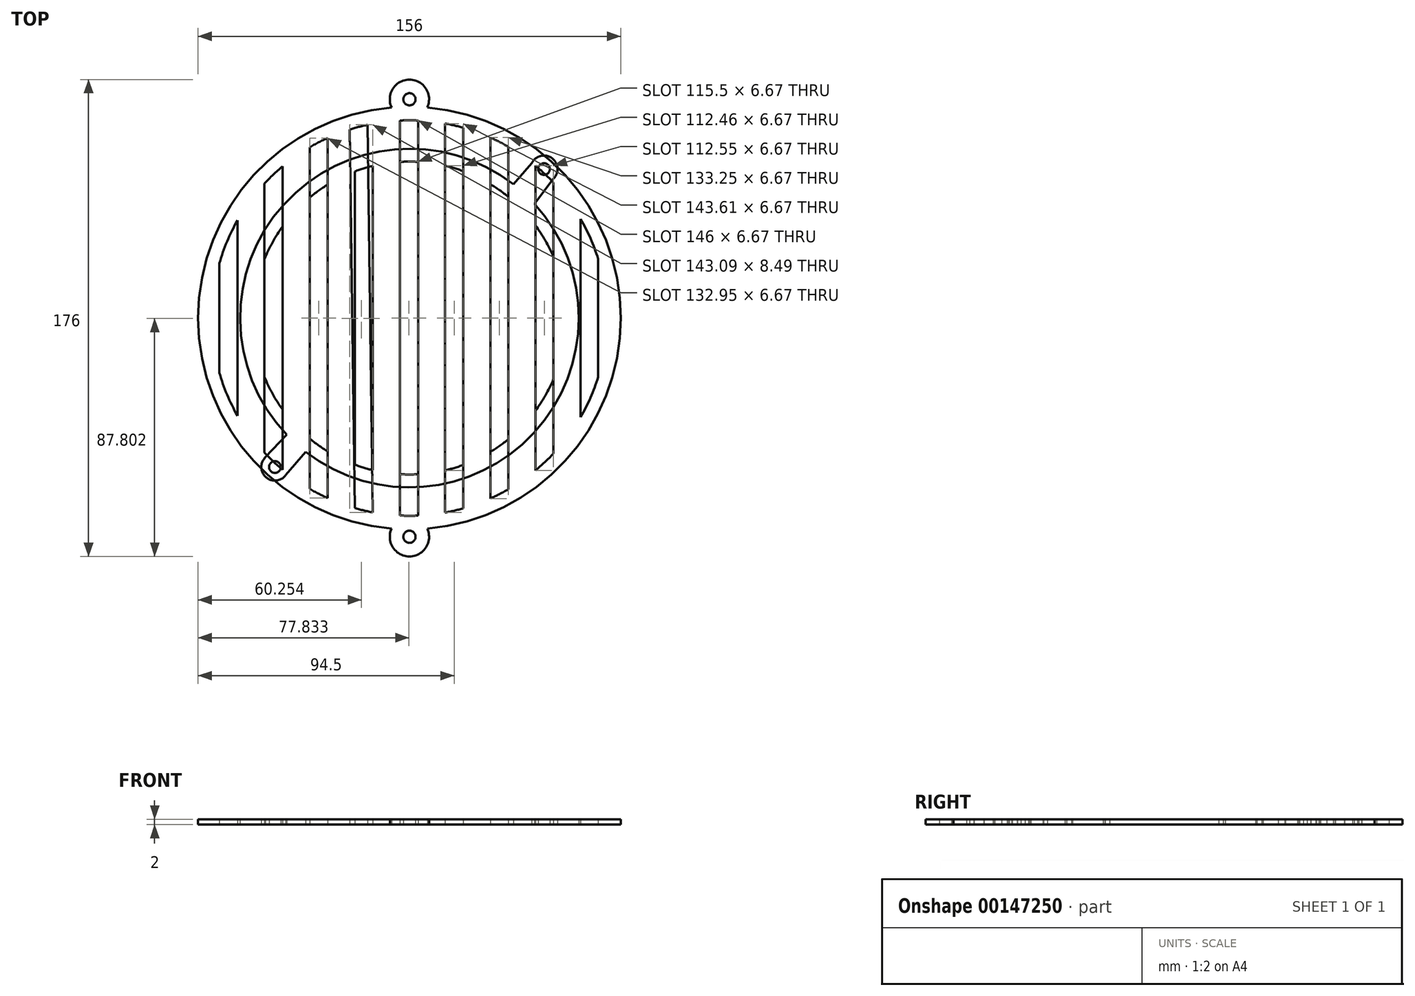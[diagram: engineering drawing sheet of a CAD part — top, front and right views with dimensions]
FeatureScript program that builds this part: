
annotation { "Feature Type Name" : "Feature", "Feature Type Description" : "" }
export const myFeature = defineFeature(function(context is Context, id is Id, definition is map)
    precondition{}
    {
        {
            var Q0;
            Q0=qCreatedBy(makeId("Top.planeOp"),FACE);
            var sketch = newSketch(context, id + "F0", { "sketchPlane" : qUnion([Q0])});
            skLineSegment(sketch, "E0.bottom", {"start": v(2, 0) * mm, "end": v(21.33, 0) * mm});
            skLineSegment(sketch, "E0.left", {"start": v(0, 2) * mm, "end": v(0, 2022) * mm});
            skLineSegment(sketch, "E0.right", {"start": v(409.5, 3.34) * mm, "end": v(409.5, 2020.66) * mm});
            skLineSegment(sketch, "E1", {"start": v(13.33, 12) * mm, "end": v(13.33, 2020) * mm, "construction": true});
            skLineSegment(sketch, "E2.0", {"start": v(23.33, 12) * mm, "end": v(23.33, 2020) * mm, "construction": true});
            skLineSegment(sketch, "E3.bottom", {"start": v(15.83, 22.83) * mm, "end": v(20.83, 22.83) * mm, "construction": true});
            skLineSegment(sketch, "E3.top", {"start": v(15.83, 17.83) * mm, "end": v(20.83, 17.83) * mm, "construction": true});
            skLineSegment(sketch, "E3.left", {"start": v(15.83, 22.83) * mm, "end": v(15.83, 17.83) * mm, "construction": true});
            skLineSegment(sketch, "E3.right", {"start": v(20.83, 22.83) * mm, "end": v(20.83, 17.83) * mm, "construction": true});
            skLineSegment(sketch, "E4", {"start": v(18.33, 17.83) * mm, "end": v(18.33, 22.83) * mm, "construction": true});
            skLineSegment(sketch, "E5", {"start": v(15.83, 20.33) * mm, "end": v(20.83, 20.33) * mm, "construction": true});
            skLineSegment(sketch, "E6", {"start": v(10, 0) * mm, "end": v(10, 28.72) * mm, "construction": true});
            skLineSegment(sketch, "E7", {"start": v(25.33, 12) * mm, "end": v(28, 12) * mm});
            skLineSegment(sketch, "E8", {"start": v(23.33, 10) * mm, "end": v(23.33, 2) * mm});
            skPoint(sketch, "E9.orphan", {"position": v(0, 12) * mm});
            skLineSegment(sketch, "E10", {"start": v(30, 10) * mm, "end": v(30, 2) * mm});
            skPoint(sketch, "E11.visualSharp", {"position": v(23.33, 12) * mm});
            skArc(sketch, "E11.filletArc", {"start": v(25.33, 12) * mm, "mid": v(23.92, 11.41) * mm, "end": v(23.33, 10) * mm});
            skPoint(sketch, "E12.visualSharp", {"position": v(30, 12) * mm});
            skArc(sketch, "E12.filletArc", {"start": v(30, 10) * mm, "mid": v(29.41, 11.41) * mm, "end": v(28, 12) * mm});
            skLineSegment(sketch, "E13.trimOffspring", {"start": v(32, 0) * mm, "end": v(38, 0) * mm});
            skPoint(sketch, "E14.visualSharp", {"position": v(23.33, 0) * mm});
            skArc(sketch, "E14.filletArc", {"start": v(21.33, 0) * mm, "mid": v(22.75, 0.59) * mm, "end": v(23.33, 2) * mm});
            skPoint(sketch, "E15.visualSharp", {"position": v(30, 0) * mm});
            skArc(sketch, "E15.filletArc", {"start": v(30, 2) * mm, "mid": v(30.59, 0.59) * mm, "end": v(32, 0) * mm});
            skLineSegment(sketch, "E16.1.0.0", {"start": v(42, 12) * mm, "end": v(44.67, 12) * mm});
            skArc(sketch, "E16.1.0.1", {"start": v(38, 0) * mm, "mid": v(39.41, 0.59) * mm, "end": v(40, 2) * mm});
            skLineSegment(sketch, "E16.1.0.2", {"start": v(40, 10) * mm, "end": v(40, 2) * mm});
            skArc(sketch, "E16.1.0.3", {"start": v(46.67, 10) * mm, "mid": v(46.08, 11.41) * mm, "end": v(44.67, 12) * mm});
            skPoint(sketch, "E16.1.0.4", {"position": v(46.67, 0) * mm});
            skPoint(sketch, "E16.1.0.5", {"position": v(40, 12) * mm});
            skPoint(sketch, "E16.1.0.6", {"position": v(40, 0) * mm});
            skLineSegment(sketch, "E16.1.0.7", {"start": v(46.67, 10) * mm, "end": v(46.67, 2) * mm});
            skArc(sketch, "E16.1.0.8", {"start": v(46.67, 2) * mm, "mid": v(47.25, 0.59) * mm, "end": v(48.67, 0) * mm});
            skArc(sketch, "E16.1.0.9", {"start": v(42, 12) * mm, "mid": v(40.59, 11.41) * mm, "end": v(40, 10) * mm});
            skPoint(sketch, "E16.1.0.10", {"position": v(46.67, 12) * mm});
            skLineSegment(sketch, "E16.1.0.11", {"start": v(48.67, 0) * mm, "end": v(54.67, 0) * mm});
            skLineSegment(sketch, "E16.2.0.0", {"start": v(58.67, 12) * mm, "end": v(61.33, 12) * mm});
            skArc(sketch, "E16.2.0.1", {"start": v(54.67, 0) * mm, "mid": v(56.08, 0.59) * mm, "end": v(56.67, 2) * mm});
            skLineSegment(sketch, "E16.2.0.2", {"start": v(56.67, 10) * mm, "end": v(56.67, 2) * mm});
            skArc(sketch, "E16.2.0.3", {"start": v(63.33, 10) * mm, "mid": v(62.75, 11.41) * mm, "end": v(61.33, 12) * mm});
            skPoint(sketch, "E16.2.0.4", {"position": v(63.33, 0) * mm});
            skPoint(sketch, "E16.2.0.5", {"position": v(56.67, 12) * mm});
            skPoint(sketch, "E16.2.0.6", {"position": v(56.67, 0) * mm});
            skLineSegment(sketch, "E16.2.0.7", {"start": v(63.33, 10) * mm, "end": v(63.33, 2) * mm});
            skArc(sketch, "E16.2.0.8", {"start": v(63.33, 2) * mm, "mid": v(63.92, 0.59) * mm, "end": v(65.33, 0) * mm});
            skArc(sketch, "E16.2.0.9", {"start": v(58.67, 12) * mm, "mid": v(57.25, 11.41) * mm, "end": v(56.67, 10) * mm});
            skPoint(sketch, "E16.2.0.10", {"position": v(63.33, 12) * mm});
            skLineSegment(sketch, "E16.2.0.11", {"start": v(65.33, 0) * mm, "end": v(71.33, 0) * mm});
            skLineSegment(sketch, "E16.3.0.0", {"start": v(75.33, 12) * mm, "end": v(78, 12) * mm});
            skArc(sketch, "E16.3.0.1", {"start": v(71.33, 0) * mm, "mid": v(72.75, 0.59) * mm, "end": v(73.33, 2) * mm});
            skLineSegment(sketch, "E16.3.0.2", {"start": v(73.33, 10) * mm, "end": v(73.33, 2) * mm});
            skArc(sketch, "E16.3.0.3", {"start": v(80, 10) * mm, "mid": v(79.41, 11.41) * mm, "end": v(78, 12) * mm});
            skPoint(sketch, "E16.3.0.4", {"position": v(80, 0) * mm});
            skPoint(sketch, "E16.3.0.5", {"position": v(73.33, 12) * mm});
            skPoint(sketch, "E16.3.0.6", {"position": v(73.33, 0) * mm});
            skLineSegment(sketch, "E16.3.0.7", {"start": v(80, 10) * mm, "end": v(80, 2) * mm});
            skArc(sketch, "E16.3.0.8", {"start": v(80, 2) * mm, "mid": v(80.59, 0.59) * mm, "end": v(82, 0) * mm});
            skArc(sketch, "E16.3.0.9", {"start": v(75.33, 12) * mm, "mid": v(73.92, 11.41) * mm, "end": v(73.33, 10) * mm});
            skPoint(sketch, "E16.3.0.10", {"position": v(80, 12) * mm});
            skLineSegment(sketch, "E16.3.0.11", {"start": v(82, 0) * mm, "end": v(88, 0) * mm});
            skLineSegment(sketch, "E16.4.0.0", {"start": v(92, 12) * mm, "end": v(94.67, 12) * mm});
            skArc(sketch, "E16.4.0.1", {"start": v(88, 0) * mm, "mid": v(89.41, 0.59) * mm, "end": v(90, 2) * mm});
            skLineSegment(sketch, "E16.4.0.2", {"start": v(90, 10) * mm, "end": v(90, 2) * mm});
            skArc(sketch, "E16.4.0.3", {"start": v(96.67, 10) * mm, "mid": v(96.08, 11.41) * mm, "end": v(94.67, 12) * mm});
            skPoint(sketch, "E16.4.0.4", {"position": v(96.67, 0) * mm});
            skPoint(sketch, "E16.4.0.5", {"position": v(90, 12) * mm});
            skPoint(sketch, "E16.4.0.6", {"position": v(90, 0) * mm});
            skLineSegment(sketch, "E16.4.0.7", {"start": v(96.67, 10) * mm, "end": v(96.67, 2) * mm});
            skArc(sketch, "E16.4.0.8", {"start": v(96.67, 2) * mm, "mid": v(97.25, 0.59) * mm, "end": v(98.67, 0) * mm});
            skArc(sketch, "E16.4.0.9", {"start": v(92, 12) * mm, "mid": v(90.59, 11.41) * mm, "end": v(90, 10) * mm});
            skPoint(sketch, "E16.4.0.10", {"position": v(96.67, 12) * mm});
            skLineSegment(sketch, "E16.4.0.11", {"start": v(98.67, 0) * mm, "end": v(104.67, 0) * mm});
            skLineSegment(sketch, "E16.5.0.0", {"start": v(108.67, 12) * mm, "end": v(111.33, 12) * mm});
            skArc(sketch, "E16.5.0.1", {"start": v(104.67, 0) * mm, "mid": v(106.08, 0.59) * mm, "end": v(106.67, 2) * mm});
            skLineSegment(sketch, "E16.5.0.2", {"start": v(106.67, 10) * mm, "end": v(106.67, 2) * mm});
            skArc(sketch, "E16.5.0.3", {"start": v(113.33, 10) * mm, "mid": v(112.75, 11.41) * mm, "end": v(111.33, 12) * mm});
            skPoint(sketch, "E16.5.0.4", {"position": v(113.33, 0) * mm});
            skPoint(sketch, "E16.5.0.5", {"position": v(106.67, 12) * mm});
            skPoint(sketch, "E16.5.0.6", {"position": v(106.67, 0) * mm});
            skLineSegment(sketch, "E16.5.0.7", {"start": v(113.33, 10) * mm, "end": v(113.33, 2) * mm});
            skArc(sketch, "E16.5.0.8", {"start": v(113.33, 2) * mm, "mid": v(113.92, 0.59) * mm, "end": v(115.33, 0) * mm});
            skArc(sketch, "E16.5.0.9", {"start": v(108.67, 12) * mm, "mid": v(107.25, 11.41) * mm, "end": v(106.67, 10) * mm});
            skPoint(sketch, "E16.5.0.10", {"position": v(113.33, 12) * mm});
            skLineSegment(sketch, "E16.5.0.11", {"start": v(115.33, 0) * mm, "end": v(121.33, 0) * mm});
            skLineSegment(sketch, "E16.6.0.0", {"start": v(125.33, 12) * mm, "end": v(128, 12) * mm});
            skArc(sketch, "E16.6.0.1", {"start": v(121.33, 0) * mm, "mid": v(122.75, 0.59) * mm, "end": v(123.33, 2) * mm});
            skLineSegment(sketch, "E16.6.0.2", {"start": v(123.33, 10) * mm, "end": v(123.33, 2) * mm});
            skArc(sketch, "E16.6.0.3", {"start": v(130, 10) * mm, "mid": v(129.41, 11.41) * mm, "end": v(128, 12) * mm});
            skPoint(sketch, "E16.6.0.4", {"position": v(130, 0) * mm});
            skPoint(sketch, "E16.6.0.5", {"position": v(123.33, 12) * mm});
            skPoint(sketch, "E16.6.0.6", {"position": v(123.33, 0) * mm});
            skLineSegment(sketch, "E16.6.0.7", {"start": v(130, 10) * mm, "end": v(130, 2) * mm});
            skArc(sketch, "E16.6.0.8", {"start": v(130, 2) * mm, "mid": v(130.59, 0.59) * mm, "end": v(132, 0) * mm});
            skArc(sketch, "E16.6.0.9", {"start": v(125.33, 12) * mm, "mid": v(123.92, 11.41) * mm, "end": v(123.33, 10) * mm});
            skPoint(sketch, "E16.6.0.10", {"position": v(130, 12) * mm});
            skLineSegment(sketch, "E16.6.0.11", {"start": v(132, 0) * mm, "end": v(138, 0) * mm});
            skLineSegment(sketch, "E16.7.0.0", {"start": v(142, 12) * mm, "end": v(144.67, 12) * mm});
            skArc(sketch, "E16.7.0.1", {"start": v(138, 0) * mm, "mid": v(139.41, 0.59) * mm, "end": v(140, 2) * mm});
            skLineSegment(sketch, "E16.7.0.2", {"start": v(140, 10) * mm, "end": v(140, 2) * mm});
            skArc(sketch, "E16.7.0.3", {"start": v(146.67, 10) * mm, "mid": v(146.08, 11.41) * mm, "end": v(144.67, 12) * mm});
            skPoint(sketch, "E16.7.0.4", {"position": v(146.67, 0) * mm});
            skPoint(sketch, "E16.7.0.5", {"position": v(140, 12) * mm});
            skPoint(sketch, "E16.7.0.6", {"position": v(140, 0) * mm});
            skLineSegment(sketch, "E16.7.0.7", {"start": v(146.67, 10) * mm, "end": v(146.67, 2) * mm});
            skArc(sketch, "E16.7.0.8", {"start": v(146.67, 2) * mm, "mid": v(147.25, 0.59) * mm, "end": v(148.67, 0) * mm});
            skArc(sketch, "E16.7.0.9", {"start": v(142, 12) * mm, "mid": v(140.59, 11.41) * mm, "end": v(140, 10) * mm});
            skPoint(sketch, "E16.7.0.10", {"position": v(146.67, 12) * mm});
            skLineSegment(sketch, "E16.7.0.11", {"start": v(148.67, 0) * mm, "end": v(154.67, 0) * mm});
            skLineSegment(sketch, "E16.8.0.0", {"start": v(158.67, 12) * mm, "end": v(161.33, 12) * mm});
            skArc(sketch, "E16.8.0.1", {"start": v(154.67, 0) * mm, "mid": v(156.08, 0.59) * mm, "end": v(156.67, 2) * mm});
            skLineSegment(sketch, "E16.8.0.2", {"start": v(156.67, 10) * mm, "end": v(156.67, 2) * mm});
            skArc(sketch, "E16.8.0.3", {"start": v(163.33, 10) * mm, "mid": v(162.75, 11.41) * mm, "end": v(161.33, 12) * mm});
            skPoint(sketch, "E16.8.0.4", {"position": v(163.33, 0) * mm});
            skPoint(sketch, "E16.8.0.5", {"position": v(156.67, 12) * mm});
            skPoint(sketch, "E16.8.0.6", {"position": v(156.67, 0) * mm});
            skLineSegment(sketch, "E16.8.0.7", {"start": v(163.33, 10) * mm, "end": v(163.33, 2) * mm});
            skArc(sketch, "E16.8.0.8", {"start": v(163.33, 2) * mm, "mid": v(163.92, 0.59) * mm, "end": v(165.33, 0) * mm});
            skArc(sketch, "E16.8.0.9", {"start": v(158.67, 12) * mm, "mid": v(157.25, 11.41) * mm, "end": v(156.67, 10) * mm});
            skPoint(sketch, "E16.8.0.10", {"position": v(163.33, 12) * mm});
            skLineSegment(sketch, "E16.8.0.11", {"start": v(165.33, 0) * mm, "end": v(171.33, 0) * mm});
            skLineSegment(sketch, "E16.9.0.0", {"start": v(175.33, 12) * mm, "end": v(178, 12) * mm});
            skArc(sketch, "E16.9.0.1", {"start": v(171.33, 0) * mm, "mid": v(172.75, 0.59) * mm, "end": v(173.33, 2) * mm});
            skLineSegment(sketch, "E16.9.0.2", {"start": v(173.33, 10) * mm, "end": v(173.33, 2) * mm});
            skArc(sketch, "E16.9.0.3", {"start": v(180, 10) * mm, "mid": v(179.41, 11.41) * mm, "end": v(178, 12) * mm});
            skPoint(sketch, "E16.9.0.4", {"position": v(180, 0) * mm});
            skPoint(sketch, "E16.9.0.5", {"position": v(173.33, 12) * mm});
            skPoint(sketch, "E16.9.0.6", {"position": v(173.33, 0) * mm});
            skLineSegment(sketch, "E16.9.0.7", {"start": v(180, 10) * mm, "end": v(180, 2) * mm});
            skArc(sketch, "E16.9.0.8", {"start": v(180, 2) * mm, "mid": v(180.59, 0.59) * mm, "end": v(182, 0) * mm});
            skArc(sketch, "E16.9.0.9", {"start": v(175.33, 12) * mm, "mid": v(173.92, 11.41) * mm, "end": v(173.33, 10) * mm});
            skPoint(sketch, "E16.9.0.10", {"position": v(180, 12) * mm});
            skLineSegment(sketch, "E16.9.0.11", {"start": v(182, 0) * mm, "end": v(188, 0) * mm});
            skLineSegment(sketch, "E16.10.0.0", {"start": v(192, 12) * mm, "end": v(194.67, 12) * mm});
            skArc(sketch, "E16.10.0.1", {"start": v(188, 0) * mm, "mid": v(189.41, 0.59) * mm, "end": v(190, 2) * mm});
            skLineSegment(sketch, "E16.10.0.2", {"start": v(190, 10) * mm, "end": v(190, 2) * mm});
            skArc(sketch, "E16.10.0.3", {"start": v(196.67, 10) * mm, "mid": v(196.08, 11.41) * mm, "end": v(194.67, 12) * mm});
            skPoint(sketch, "E16.10.0.4", {"position": v(196.67, 0) * mm});
            skPoint(sketch, "E16.10.0.5", {"position": v(190, 12) * mm});
            skPoint(sketch, "E16.10.0.6", {"position": v(190, 0) * mm});
            skLineSegment(sketch, "E16.10.0.7", {"start": v(196.67, 10) * mm, "end": v(196.67, 2) * mm});
            skArc(sketch, "E16.10.0.8", {"start": v(196.67, 2) * mm, "mid": v(197.25, 0.59) * mm, "end": v(198.67, 0) * mm});
            skArc(sketch, "E16.10.0.9", {"start": v(192, 12) * mm, "mid": v(190.59, 11.41) * mm, "end": v(190, 10) * mm});
            skPoint(sketch, "E16.10.0.10", {"position": v(196.67, 12) * mm});
            skLineSegment(sketch, "E16.10.0.11", {"start": v(198.67, 0) * mm, "end": v(204.67, 0) * mm});
            skLineSegment(sketch, "E16.11.0.0", {"start": v(208.67, 12) * mm, "end": v(211.33, 12) * mm});
            skArc(sketch, "E16.11.0.1", {"start": v(204.67, 0) * mm, "mid": v(206.08, 0.59) * mm, "end": v(206.67, 2) * mm});
            skLineSegment(sketch, "E16.11.0.2", {"start": v(206.67, 10) * mm, "end": v(206.67, 2) * mm});
            skArc(sketch, "E16.11.0.3", {"start": v(213.33, 10) * mm, "mid": v(212.75, 11.41) * mm, "end": v(211.33, 12) * mm});
            skPoint(sketch, "E16.11.0.4", {"position": v(213.33, 0) * mm});
            skPoint(sketch, "E16.11.0.5", {"position": v(206.67, 12) * mm});
            skPoint(sketch, "E16.11.0.6", {"position": v(206.67, 0) * mm});
            skLineSegment(sketch, "E16.11.0.7", {"start": v(213.33, 10) * mm, "end": v(213.33, 2) * mm});
            skArc(sketch, "E16.11.0.8", {"start": v(213.33, 2) * mm, "mid": v(213.92, 0.59) * mm, "end": v(215.33, 0) * mm});
            skArc(sketch, "E16.11.0.9", {"start": v(208.67, 12) * mm, "mid": v(207.25, 11.41) * mm, "end": v(206.67, 10) * mm});
            skPoint(sketch, "E16.11.0.10", {"position": v(213.33, 12) * mm});
            skLineSegment(sketch, "E16.11.0.11", {"start": v(215.33, 0) * mm, "end": v(221.33, 0) * mm});
            skLineSegment(sketch, "E16.12.0.0", {"start": v(225.33, 12) * mm, "end": v(228, 12) * mm});
            skArc(sketch, "E16.12.0.1", {"start": v(221.33, 0) * mm, "mid": v(222.75, 0.59) * mm, "end": v(223.33, 2) * mm});
            skLineSegment(sketch, "E16.12.0.2", {"start": v(223.33, 10) * mm, "end": v(223.33, 2) * mm});
            skArc(sketch, "E16.12.0.3", {"start": v(230, 10) * mm, "mid": v(229.41, 11.41) * mm, "end": v(228, 12) * mm});
            skPoint(sketch, "E16.12.0.4", {"position": v(230, 0) * mm});
            skPoint(sketch, "E16.12.0.5", {"position": v(223.33, 12) * mm});
            skPoint(sketch, "E16.12.0.6", {"position": v(223.33, 0) * mm});
            skLineSegment(sketch, "E16.12.0.7", {"start": v(230, 10) * mm, "end": v(230, 2) * mm});
            skArc(sketch, "E16.12.0.8", {"start": v(230, 2) * mm, "mid": v(230.59, 0.59) * mm, "end": v(232, 0) * mm});
            skArc(sketch, "E16.12.0.9", {"start": v(225.33, 12) * mm, "mid": v(223.92, 11.41) * mm, "end": v(223.33, 10) * mm});
            skPoint(sketch, "E16.12.0.10", {"position": v(230, 12) * mm});
            skLineSegment(sketch, "E16.12.0.11", {"start": v(232, 0) * mm, "end": v(238, 0) * mm});
            skLineSegment(sketch, "E16.13.0.0", {"start": v(242, 12) * mm, "end": v(244.67, 12) * mm});
            skArc(sketch, "E16.13.0.1", {"start": v(238, 0) * mm, "mid": v(239.41, 0.59) * mm, "end": v(240, 2) * mm});
            skLineSegment(sketch, "E16.13.0.2", {"start": v(240, 10) * mm, "end": v(240, 2) * mm});
            skArc(sketch, "E16.13.0.3", {"start": v(246.67, 10) * mm, "mid": v(246.08, 11.41) * mm, "end": v(244.67, 12) * mm});
            skPoint(sketch, "E16.13.0.4", {"position": v(246.67, 0) * mm});
            skPoint(sketch, "E16.13.0.5", {"position": v(240, 12) * mm});
            skPoint(sketch, "E16.13.0.6", {"position": v(240, 0) * mm});
            skLineSegment(sketch, "E16.13.0.7", {"start": v(246.67, 10) * mm, "end": v(246.67, 2) * mm});
            skArc(sketch, "E16.13.0.8", {"start": v(246.67, 2) * mm, "mid": v(247.25, 0.59) * mm, "end": v(248.67, 0) * mm});
            skArc(sketch, "E16.13.0.9", {"start": v(242, 12) * mm, "mid": v(240.59, 11.41) * mm, "end": v(240, 10) * mm});
            skPoint(sketch, "E16.13.0.10", {"position": v(246.67, 12) * mm});
            skLineSegment(sketch, "E16.13.0.11", {"start": v(248.67, 0) * mm, "end": v(254.67, 0) * mm});
            skLineSegment(sketch, "E16.14.0.0", {"start": v(258.67, 12) * mm, "end": v(261.33, 12) * mm});
            skArc(sketch, "E16.14.0.1", {"start": v(254.67, 0) * mm, "mid": v(256.08, 0.59) * mm, "end": v(256.67, 2) * mm});
            skLineSegment(sketch, "E16.14.0.2", {"start": v(256.67, 10) * mm, "end": v(256.67, 2) * mm});
            skArc(sketch, "E16.14.0.3", {"start": v(263.33, 10) * mm, "mid": v(262.75, 11.41) * mm, "end": v(261.33, 12) * mm});
            skPoint(sketch, "E16.14.0.4", {"position": v(263.33, 0) * mm});
            skPoint(sketch, "E16.14.0.5", {"position": v(256.67, 12) * mm});
            skPoint(sketch, "E16.14.0.6", {"position": v(256.67, 0) * mm});
            skLineSegment(sketch, "E16.14.0.7", {"start": v(263.33, 10) * mm, "end": v(263.33, 2) * mm});
            skArc(sketch, "E16.14.0.8", {"start": v(263.33, 2) * mm, "mid": v(263.92, 0.59) * mm, "end": v(265.33, 0) * mm});
            skArc(sketch, "E16.14.0.9", {"start": v(258.67, 12) * mm, "mid": v(257.25, 11.41) * mm, "end": v(256.67, 10) * mm});
            skPoint(sketch, "E16.14.0.10", {"position": v(263.33, 12) * mm});
            skLineSegment(sketch, "E16.14.0.11", {"start": v(265.33, 0) * mm, "end": v(271.33, 0) * mm});
            skLineSegment(sketch, "E16.15.0.0", {"start": v(275.33, 12) * mm, "end": v(278, 12) * mm});
            skArc(sketch, "E16.15.0.1", {"start": v(271.33, 0) * mm, "mid": v(272.75, 0.59) * mm, "end": v(273.33, 2) * mm});
            skLineSegment(sketch, "E16.15.0.2", {"start": v(273.33, 10) * mm, "end": v(273.33, 2) * mm});
            skArc(sketch, "E16.15.0.3", {"start": v(280, 10) * mm, "mid": v(279.41, 11.41) * mm, "end": v(278, 12) * mm});
            skPoint(sketch, "E16.15.0.4", {"position": v(280, 0) * mm});
            skPoint(sketch, "E16.15.0.5", {"position": v(273.33, 12) * mm});
            skPoint(sketch, "E16.15.0.6", {"position": v(273.33, 0) * mm});
            skLineSegment(sketch, "E16.15.0.7", {"start": v(280, 10) * mm, "end": v(280, 2) * mm});
            skArc(sketch, "E16.15.0.8", {"start": v(280, 2) * mm, "mid": v(280.59, 0.59) * mm, "end": v(282, 0) * mm});
            skArc(sketch, "E16.15.0.9", {"start": v(275.33, 12) * mm, "mid": v(273.92, 11.41) * mm, "end": v(273.33, 10) * mm});
            skPoint(sketch, "E16.15.0.10", {"position": v(280, 12) * mm});
            skLineSegment(sketch, "E16.15.0.11", {"start": v(282, 0) * mm, "end": v(288, 0) * mm});
            skLineSegment(sketch, "E16.16.0.0", {"start": v(292, 12) * mm, "end": v(294.67, 12) * mm});
            skArc(sketch, "E16.16.0.1", {"start": v(288, 0) * mm, "mid": v(289.41, 0.59) * mm, "end": v(290, 2) * mm});
            skLineSegment(sketch, "E16.16.0.2", {"start": v(290, 10) * mm, "end": v(290, 2) * mm});
            skArc(sketch, "E16.16.0.3", {"start": v(296.67, 10) * mm, "mid": v(296.08, 11.41) * mm, "end": v(294.67, 12) * mm});
            skPoint(sketch, "E16.16.0.4", {"position": v(296.67, 0) * mm});
            skPoint(sketch, "E16.16.0.5", {"position": v(290, 12) * mm});
            skPoint(sketch, "E16.16.0.6", {"position": v(290, 0) * mm});
            skLineSegment(sketch, "E16.16.0.7", {"start": v(296.67, 10) * mm, "end": v(296.67, 2) * mm});
            skArc(sketch, "E16.16.0.8", {"start": v(296.67, 2) * mm, "mid": v(297.25, 0.59) * mm, "end": v(298.67, 0) * mm});
            skArc(sketch, "E16.16.0.9", {"start": v(292, 12) * mm, "mid": v(290.59, 11.41) * mm, "end": v(290, 10) * mm});
            skPoint(sketch, "E16.16.0.10", {"position": v(296.67, 12) * mm});
            skLineSegment(sketch, "E16.16.0.11", {"start": v(298.67, 0) * mm, "end": v(304.67, 0) * mm});
            skLineSegment(sketch, "E16.17.0.0", {"start": v(308.67, 12) * mm, "end": v(311.33, 12) * mm});
            skArc(sketch, "E16.17.0.1", {"start": v(304.67, 0) * mm, "mid": v(306.08, 0.59) * mm, "end": v(306.67, 2) * mm});
            skLineSegment(sketch, "E16.17.0.2", {"start": v(306.67, 10) * mm, "end": v(306.67, 2) * mm});
            skArc(sketch, "E16.17.0.3", {"start": v(313.33, 10) * mm, "mid": v(312.75, 11.41) * mm, "end": v(311.33, 12) * mm});
            skPoint(sketch, "E16.17.0.4", {"position": v(313.33, 0) * mm});
            skPoint(sketch, "E16.17.0.5", {"position": v(306.67, 12) * mm});
            skPoint(sketch, "E16.17.0.6", {"position": v(306.67, 0) * mm});
            skLineSegment(sketch, "E16.17.0.7", {"start": v(313.33, 10) * mm, "end": v(313.33, 2) * mm});
            skArc(sketch, "E16.17.0.8", {"start": v(313.33, 2) * mm, "mid": v(313.92, 0.59) * mm, "end": v(315.33, 0) * mm});
            skArc(sketch, "E16.17.0.9", {"start": v(308.67, 12) * mm, "mid": v(307.25, 11.41) * mm, "end": v(306.67, 10) * mm});
            skPoint(sketch, "E16.17.0.10", {"position": v(313.33, 12) * mm});
            skLineSegment(sketch, "E16.17.0.11", {"start": v(315.33, 0) * mm, "end": v(321.33, 0) * mm});
            skLineSegment(sketch, "E16.18.0.0", {"start": v(325.33, 12) * mm, "end": v(328, 12) * mm});
            skArc(sketch, "E16.18.0.1", {"start": v(321.33, 0) * mm, "mid": v(322.75, 0.59) * mm, "end": v(323.33, 2) * mm});
            skLineSegment(sketch, "E16.18.0.2", {"start": v(323.33, 10) * mm, "end": v(323.33, 2) * mm});
            skArc(sketch, "E16.18.0.3", {"start": v(330, 10) * mm, "mid": v(329.41, 11.41) * mm, "end": v(328, 12) * mm});
            skPoint(sketch, "E16.18.0.4", {"position": v(330, 0) * mm});
            skPoint(sketch, "E16.18.0.5", {"position": v(323.33, 12) * mm});
            skPoint(sketch, "E16.18.0.6", {"position": v(323.33, 0) * mm});
            skLineSegment(sketch, "E16.18.0.7", {"start": v(330, 10) * mm, "end": v(330, 2) * mm});
            skArc(sketch, "E16.18.0.8", {"start": v(330, 2) * mm, "mid": v(330.59, 0.59) * mm, "end": v(332, 0) * mm});
            skArc(sketch, "E16.18.0.9", {"start": v(325.33, 12) * mm, "mid": v(323.92, 11.41) * mm, "end": v(323.33, 10) * mm});
            skPoint(sketch, "E16.18.0.10", {"position": v(330, 12) * mm});
            skLineSegment(sketch, "E16.18.0.11", {"start": v(332, 0) * mm, "end": v(338, 0) * mm});
            skLineSegment(sketch, "E16.19.0.0", {"start": v(342, 12) * mm, "end": v(344.67, 12) * mm});
            skArc(sketch, "E16.19.0.1", {"start": v(338, 0) * mm, "mid": v(339.41, 0.59) * mm, "end": v(340, 2) * mm});
            skLineSegment(sketch, "E16.19.0.2", {"start": v(340, 10) * mm, "end": v(340, 2) * mm});
            skArc(sketch, "E16.19.0.3", {"start": v(346.67, 10) * mm, "mid": v(346.08, 11.41) * mm, "end": v(344.67, 12) * mm});
            skPoint(sketch, "E16.19.0.4", {"position": v(346.67, 0) * mm});
            skPoint(sketch, "E16.19.0.5", {"position": v(340, 12) * mm});
            skPoint(sketch, "E16.19.0.6", {"position": v(340, 0) * mm});
            skLineSegment(sketch, "E16.19.0.7", {"start": v(346.67, 10) * mm, "end": v(346.67, 2) * mm});
            skArc(sketch, "E16.19.0.8", {"start": v(346.67, 2) * mm, "mid": v(347.25, 0.59) * mm, "end": v(348.67, 0) * mm});
            skArc(sketch, "E16.19.0.9", {"start": v(342, 12) * mm, "mid": v(340.59, 11.41) * mm, "end": v(340, 10) * mm});
            skPoint(sketch, "E16.19.0.10", {"position": v(346.67, 12) * mm});
            skLineSegment(sketch, "E16.19.0.11", {"start": v(348.67, 0) * mm, "end": v(354.67, 0) * mm});
            skLineSegment(sketch, "E16.20.0.0", {"start": v(358.67, 12) * mm, "end": v(361.33, 12) * mm});
            skArc(sketch, "E16.20.0.1", {"start": v(354.67, 0) * mm, "mid": v(356.08, 0.59) * mm, "end": v(356.67, 2) * mm});
            skLineSegment(sketch, "E16.20.0.2", {"start": v(356.67, 10) * mm, "end": v(356.67, 2) * mm});
            skArc(sketch, "E16.20.0.3", {"start": v(363.33, 10) * mm, "mid": v(362.75, 11.41) * mm, "end": v(361.33, 12) * mm});
            skPoint(sketch, "E16.20.0.4", {"position": v(363.33, 0) * mm});
            skPoint(sketch, "E16.20.0.5", {"position": v(356.67, 12) * mm});
            skPoint(sketch, "E16.20.0.6", {"position": v(356.67, 0) * mm});
            skLineSegment(sketch, "E16.20.0.7", {"start": v(363.33, 10) * mm, "end": v(363.33, 2) * mm});
            skArc(sketch, "E16.20.0.8", {"start": v(363.33, 2) * mm, "mid": v(363.92, 0.59) * mm, "end": v(365.33, 0) * mm});
            skArc(sketch, "E16.20.0.9", {"start": v(358.67, 12) * mm, "mid": v(357.25, 11.41) * mm, "end": v(356.67, 10) * mm});
            skPoint(sketch, "E16.20.0.10", {"position": v(363.33, 12) * mm});
            skLineSegment(sketch, "E16.20.0.11", {"start": v(365.33, 0) * mm, "end": v(371.33, 0) * mm});
            skLineSegment(sketch, "E16.21.0.0", {"start": v(375.33, 12) * mm, "end": v(378, 12) * mm});
            skArc(sketch, "E16.21.0.1", {"start": v(371.33, 0) * mm, "mid": v(372.75, 0.59) * mm, "end": v(373.33, 2) * mm});
            skLineSegment(sketch, "E16.21.0.2", {"start": v(373.33, 10) * mm, "end": v(373.33, 2) * mm});
            skArc(sketch, "E16.21.0.3", {"start": v(380, 10) * mm, "mid": v(379.41, 11.41) * mm, "end": v(378, 12) * mm});
            skPoint(sketch, "E16.21.0.4", {"position": v(380, 0) * mm});
            skPoint(sketch, "E16.21.0.5", {"position": v(373.33, 12) * mm});
            skPoint(sketch, "E16.21.0.6", {"position": v(373.33, 0) * mm});
            skLineSegment(sketch, "E16.21.0.7", {"start": v(380, 10) * mm, "end": v(380, 2) * mm});
            skArc(sketch, "E16.21.0.8", {"start": v(380, 2) * mm, "mid": v(380.59, 0.59) * mm, "end": v(382, 0) * mm});
            skArc(sketch, "E16.21.0.9", {"start": v(375.33, 12) * mm, "mid": v(373.92, 11.41) * mm, "end": v(373.33, 10) * mm});
            skPoint(sketch, "E16.21.0.10", {"position": v(380, 12) * mm});
            skLineSegment(sketch, "E16.21.0.11", {"start": v(382, 0) * mm, "end": v(388, 0) * mm});
            skLineSegment(sketch, "E16.22.0.0", {"start": v(392, 12) * mm, "end": v(394.67, 12) * mm});
            skArc(sketch, "E16.22.0.1", {"start": v(388, 0) * mm, "mid": v(389.41, 0.59) * mm, "end": v(390, 2) * mm});
            skLineSegment(sketch, "E16.22.0.2", {"start": v(390, 10) * mm, "end": v(390, 2) * mm});
            skArc(sketch, "E16.22.0.3", {"start": v(396.67, 10) * mm, "mid": v(396.08, 11.41) * mm, "end": v(394.67, 12) * mm});
            skPoint(sketch, "E16.22.0.4", {"position": v(396.67, 0) * mm});
            skPoint(sketch, "E16.22.0.5", {"position": v(390, 12) * mm});
            skPoint(sketch, "E16.22.0.6", {"position": v(390, 0) * mm});
            skLineSegment(sketch, "E16.22.0.7", {"start": v(396.67, 10) * mm, "end": v(396.67, 2) * mm});
            skArc(sketch, "E16.22.0.8", {"start": v(396.67, 2) * mm, "mid": v(397.25, 0.59) * mm, "end": v(398.67, 0) * mm});
            skArc(sketch, "E16.22.0.9", {"start": v(392, 12) * mm, "mid": v(390.59, 11.41) * mm, "end": v(390, 10) * mm});
            skPoint(sketch, "E16.22.0.10", {"position": v(396.67, 12) * mm});
            skLineSegment(sketch, "E16.22.0.11", {"start": v(398.67, 0) * mm, "end": v(404.67, 0) * mm});
            skLineSegment(sketch, "E16.direction1", {"start": v(21.33, 0) * mm, "end": v(38, 0) * mm, "construction": true});
            skLineSegment(sketch, "E17", {"start": v(404.67, 0) * mm, "end": v(408.26, 1.49) * mm});
            skLineSegment(sketch, "E18", {"start": v(409.5, 1012) * mm, "end": v(322.2, 1012) * mm, "construction": true});
            skPoint(sketch, "E18.endSnap0", {"position": v(409.5, 1012) * mm});
            skLineSegment(sketch, "E19.MirrorCS", {"start": v(198.67, 2024) * mm, "end": v(204.67, 2024) * mm});
            skLineSegment(sketch, "E20.MirrorCS", {"start": v(175.33, 2012) * mm, "end": v(178, 2012) * mm});
            skLineSegment(sketch, "E21.MirrorCS", {"start": v(208.67, 2012) * mm, "end": v(211.33, 2012) * mm});
            skLineSegment(sketch, "E22.MirrorCS", {"start": v(165.33, 2024) * mm, "end": v(171.33, 2024) * mm});
            skLineSegment(sketch, "E23.MirrorCS", {"start": v(140, 2014) * mm, "end": v(140, 2022) * mm});
            skLineSegment(sketch, "E24.MirrorCS", {"start": v(192, 2012) * mm, "end": v(194.67, 2012) * mm});
            skLineSegment(sketch, "E25.MirrorCS", {"start": v(158.67, 2012) * mm, "end": v(161.33, 2012) * mm});
            skLineSegment(sketch, "E26.MirrorCS", {"start": v(125.33, 2012) * mm, "end": v(128, 2012) * mm});
            skLineSegment(sketch, "E27.MirrorCS", {"start": v(173.33, 2014) * mm, "end": v(173.33, 2022) * mm});
            skLineSegment(sketch, "E28.MirrorCS", {"start": v(132, 2024) * mm, "end": v(138, 2024) * mm});
            skLineSegment(sketch, "E29.MirrorCS", {"start": v(142, 2012) * mm, "end": v(144.67, 2012) * mm});
            skArc(sketch, "E30.MirrorCS", {"start": v(204.67, 2024) * mm, "mid": v(206.08, 2023.41) * mm, "end": v(206.67, 2022) * mm});
            skLineSegment(sketch, "E31.MirrorCS", {"start": v(108.67, 2012) * mm, "end": v(111.33, 2012) * mm});
            skLineSegment(sketch, "E32.MirrorCS", {"start": v(130, 2014) * mm, "end": v(130, 2022) * mm});
            skLineSegment(sketch, "E33.MirrorCS", {"start": v(163.33, 2014) * mm, "end": v(163.33, 2022) * mm});
            skArc(sketch, "E34.MirrorCS", {"start": v(196.67, 2014) * mm, "mid": v(196.08, 2012.59) * mm, "end": v(194.67, 2012) * mm});
            skArc(sketch, "E35.MirrorCS", {"start": v(163.33, 2014) * mm, "mid": v(162.75, 2012.59) * mm, "end": v(161.33, 2012) * mm});
            skArc(sketch, "E36.MirrorCS", {"start": v(130, 2014) * mm, "mid": v(129.41, 2012.59) * mm, "end": v(128, 2012) * mm});
            skLineSegment(sketch, "E37.MirrorCS", {"start": v(242, 2012) * mm, "end": v(244.67, 2012) * mm});
            skLineSegment(sketch, "E38.MirrorCS", {"start": v(206.67, 2014) * mm, "end": v(206.67, 2022) * mm});
            skLineSegment(sketch, "E39.MirrorCS", {"start": v(225.33, 2012) * mm, "end": v(228, 2012) * mm});
            skArc(sketch, "E40.MirrorCS", {"start": v(138, 2024) * mm, "mid": v(139.41, 2023.41) * mm, "end": v(140, 2022) * mm});
            skLineSegment(sketch, "E41.MirrorCS", {"start": v(232, 2024) * mm, "end": v(238, 2024) * mm});
            skArc(sketch, "E42.MirrorCS", {"start": v(171.33, 2024) * mm, "mid": v(172.75, 2023.41) * mm, "end": v(173.33, 2022) * mm});
            skLineSegment(sketch, "E43.MirrorCS", {"start": v(98.67, 2024) * mm, "end": v(104.67, 2024) * mm});
            skLineSegment(sketch, "E44.MirrorCS", {"start": v(148.67, 2024) * mm, "end": v(154.67, 2024) * mm});
            skLineSegment(sketch, "E45.MirrorCS", {"start": v(182, 2024) * mm, "end": v(188, 2024) * mm});
            skLineSegment(sketch, "E46.MirrorCS", {"start": v(215.33, 2024) * mm, "end": v(221.33, 2024) * mm});
            skLineSegment(sketch, "E47.MirrorCS", {"start": v(115.33, 2024) * mm, "end": v(121.33, 2024) * mm});
            skLineSegment(sketch, "E48.MirrorCS", {"start": v(106.67, 2014) * mm, "end": v(106.67, 2022) * mm});
            skArc(sketch, "E49.MirrorCS", {"start": v(146.67, 2014) * mm, "mid": v(146.08, 2012.59) * mm, "end": v(144.67, 2012) * mm});
            skArc(sketch, "E50.MirrorCS", {"start": v(180, 2014) * mm, "mid": v(179.41, 2012.59) * mm, "end": v(178, 2012) * mm});
            skLineSegment(sketch, "E51.MirrorCS", {"start": v(146.67, 2014) * mm, "end": v(146.67, 2022) * mm});
            skLineSegment(sketch, "E52.MirrorCS", {"start": v(180, 2014) * mm, "end": v(180, 2022) * mm});
            skArc(sketch, "E53.MirrorCS", {"start": v(213.33, 2014) * mm, "mid": v(212.75, 2012.59) * mm, "end": v(211.33, 2012) * mm});
            skLineSegment(sketch, "E54.MirrorCS", {"start": v(213.33, 2014) * mm, "end": v(213.33, 2022) * mm});
            skLineSegment(sketch, "E55.MirrorCS", {"start": v(113.33, 2014) * mm, "end": v(113.33, 2022) * mm});
            skArc(sketch, "E56.MirrorCS", {"start": v(113.33, 2014) * mm, "mid": v(112.75, 2012.59) * mm, "end": v(111.33, 2012) * mm});
            skArc(sketch, "E57.MirrorCS", {"start": v(125.33, 2012) * mm, "mid": v(123.92, 2012.59) * mm, "end": v(123.33, 2014) * mm});
            skArc(sketch, "E58.MirrorCS", {"start": v(158.67, 2012) * mm, "mid": v(157.25, 2012.59) * mm, "end": v(156.67, 2014) * mm});
            skLineSegment(sketch, "E59.MirrorCS", {"start": v(265.33, 2024) * mm, "end": v(271.33, 2024) * mm});
            skLineSegment(sketch, "E60.MirrorCS", {"start": v(96.67, 2014) * mm, "end": v(96.67, 2022) * mm});
            skLineSegment(sketch, "E61.MirrorCS", {"start": v(196.67, 2014) * mm, "end": v(196.67, 2022) * mm});
            skArc(sketch, "E62.MirrorCS", {"start": v(230, 2014) * mm, "mid": v(229.41, 2012.59) * mm, "end": v(228, 2012) * mm});
            skLineSegment(sketch, "E63.MirrorCS", {"start": v(275.33, 2012) * mm, "end": v(278, 2012) * mm});
            skArc(sketch, "E64.MirrorCS", {"start": v(238, 2024) * mm, "mid": v(239.41, 2023.41) * mm, "end": v(240, 2022) * mm});
            skArc(sketch, "E65.MirrorCS", {"start": v(104.67, 2024) * mm, "mid": v(106.08, 2023.41) * mm, "end": v(106.67, 2022) * mm});
            skArc(sketch, "E66.MirrorCS", {"start": v(196.67, 2022) * mm, "mid": v(197.25, 2023.41) * mm, "end": v(198.67, 2024) * mm});
            skLineSegment(sketch, "E67.MirrorCS", {"start": v(190, 2014) * mm, "end": v(190, 2022) * mm});
            skLineSegment(sketch, "E68.MirrorCS", {"start": v(223.33, 2014) * mm, "end": v(223.33, 2022) * mm});
            skArc(sketch, "E69.MirrorCS", {"start": v(163.33, 2022) * mm, "mid": v(163.92, 2023.41) * mm, "end": v(165.33, 2024) * mm});
            skLineSegment(sketch, "E70.MirrorCS", {"start": v(156.67, 2014) * mm, "end": v(156.67, 2022) * mm});
            skLineSegment(sketch, "E71.MirrorCS", {"start": v(258.67, 2012) * mm, "end": v(261.33, 2012) * mm});
            skLineSegment(sketch, "E72.MirrorCS", {"start": v(92, 2012) * mm, "end": v(94.67, 2012) * mm});
            skArc(sketch, "E73.MirrorCS", {"start": v(192, 2012) * mm, "mid": v(190.59, 2012.59) * mm, "end": v(190, 2014) * mm});
            skLineSegment(sketch, "E74.MirrorCS", {"start": v(123.33, 2014) * mm, "end": v(123.33, 2022) * mm});
            skLineSegment(sketch, "E75.MirrorCS", {"start": v(273.33, 2014) * mm, "end": v(273.33, 2022) * mm});
            skLineSegment(sketch, "E76.MirrorCS", {"start": v(240, 2014) * mm, "end": v(240, 2022) * mm});
            skArc(sketch, "E77.MirrorCS", {"start": v(188, 2024) * mm, "mid": v(189.41, 2023.41) * mm, "end": v(190, 2022) * mm});
            skArc(sketch, "E78.MirrorCS", {"start": v(221.33, 2024) * mm, "mid": v(222.75, 2023.41) * mm, "end": v(223.33, 2022) * mm});
            skArc(sketch, "E79.MirrorCS", {"start": v(154.67, 2024) * mm, "mid": v(156.08, 2023.41) * mm, "end": v(156.67, 2022) * mm});
            skLineSegment(sketch, "E80.MirrorCS", {"start": v(248.67, 2024) * mm, "end": v(254.67, 2024) * mm});
            skArc(sketch, "E81.MirrorCS", {"start": v(130, 2022) * mm, "mid": v(130.59, 2023.41) * mm, "end": v(132, 2024) * mm});
            skArc(sketch, "E82.MirrorCS", {"start": v(121.33, 2024) * mm, "mid": v(122.75, 2023.41) * mm, "end": v(123.33, 2022) * mm});
            skArc(sketch, "E83.MirrorCS", {"start": v(246.67, 2014) * mm, "mid": v(246.08, 2012.59) * mm, "end": v(244.67, 2012) * mm});
            skArc(sketch, "E84.MirrorCS", {"start": v(142, 2012) * mm, "mid": v(140.59, 2012.59) * mm, "end": v(140, 2014) * mm});
            skArc(sketch, "E85.MirrorCS", {"start": v(208.67, 2012) * mm, "mid": v(207.25, 2012.59) * mm, "end": v(206.67, 2014) * mm});
            skArc(sketch, "E86.MirrorCS", {"start": v(180, 2022) * mm, "mid": v(180.59, 2023.41) * mm, "end": v(182, 2024) * mm});
            skArc(sketch, "E87.MirrorCS", {"start": v(213.33, 2022) * mm, "mid": v(213.92, 2023.41) * mm, "end": v(215.33, 2024) * mm});
            skArc(sketch, "E88.MirrorCS", {"start": v(113.33, 2022) * mm, "mid": v(113.92, 2023.41) * mm, "end": v(115.33, 2024) * mm});
            skArc(sketch, "E89.MirrorCS", {"start": v(175.33, 2012) * mm, "mid": v(173.92, 2012.59) * mm, "end": v(173.33, 2014) * mm});
            skArc(sketch, "E90.MirrorCS", {"start": v(146.67, 2022) * mm, "mid": v(147.25, 2023.41) * mm, "end": v(148.67, 2024) * mm});
            skLineSegment(sketch, "E91.MirrorCS", {"start": v(246.67, 2014) * mm, "end": v(246.67, 2022) * mm});
            skArc(sketch, "E92.MirrorCS", {"start": v(271.33, 2024) * mm, "mid": v(272.75, 2023.41) * mm, "end": v(273.33, 2022) * mm});
            skLineSegment(sketch, "E93.MirrorCS", {"start": v(75.33, 2012) * mm, "end": v(78, 2012) * mm});
            skLineSegment(sketch, "E94.MirrorCS", {"start": v(306.67, 2014) * mm, "end": v(306.67, 2022) * mm});
            skLineSegment(sketch, "E95.MirrorCS", {"start": v(298.67, 2024) * mm, "end": v(304.67, 2024) * mm});
            skLineSegment(sketch, "E96.MirrorCS", {"start": v(230, 2014) * mm, "end": v(230, 2022) * mm});
            skLineSegment(sketch, "E97.MirrorCS", {"start": v(263.33, 2014) * mm, "end": v(263.33, 2022) * mm});
            skArc(sketch, "E98.MirrorCS", {"start": v(263.33, 2014) * mm, "mid": v(262.75, 2012.59) * mm, "end": v(261.33, 2012) * mm});
            skArc(sketch, "E99.MirrorCS", {"start": v(96.67, 2014) * mm, "mid": v(96.08, 2012.59) * mm, "end": v(94.67, 2012) * mm});
            skArc(sketch, "E100.MirrorCS", {"start": v(230, 2022) * mm, "mid": v(230.59, 2023.41) * mm, "end": v(232, 2024) * mm});
            skLineSegment(sketch, "E101.MirrorCS", {"start": v(256.67, 2014) * mm, "end": v(256.67, 2022) * mm});
            skArc(sketch, "E102.MirrorCS", {"start": v(96.67, 2022) * mm, "mid": v(97.25, 2023.41) * mm, "end": v(98.67, 2024) * mm});
            skLineSegment(sketch, "E103.MirrorCS", {"start": v(292, 2012) * mm, "end": v(294.67, 2012) * mm});
            skArc(sketch, "E104.MirrorCS", {"start": v(225.33, 2012) * mm, "mid": v(223.92, 2012.59) * mm, "end": v(223.33, 2014) * mm});
            skLineSegment(sketch, "E105.MirrorCS", {"start": v(308.67, 2012) * mm, "end": v(311.33, 2012) * mm});
            skArc(sketch, "E106.MirrorCS", {"start": v(254.67, 2024) * mm, "mid": v(256.08, 2023.41) * mm, "end": v(256.67, 2022) * mm});
            skLineSegment(sketch, "E107.MirrorCS", {"start": v(82, 2024) * mm, "end": v(88, 2024) * mm});
            skLineSegment(sketch, "E108.MirrorCS", {"start": v(282, 2024) * mm, "end": v(288, 2024) * mm});
            skArc(sketch, "E109.MirrorCS", {"start": v(280, 2014) * mm, "mid": v(279.41, 2012.59) * mm, "end": v(278, 2012) * mm});
            skLineSegment(sketch, "E110.MirrorCS", {"start": v(80, 2014) * mm, "end": v(80, 2022) * mm});
            skArc(sketch, "E111.MirrorCS", {"start": v(242, 2012) * mm, "mid": v(240.59, 2012.59) * mm, "end": v(240, 2014) * mm});
            skArc(sketch, "E112.MirrorCS", {"start": v(108.67, 2012) * mm, "mid": v(107.25, 2012.59) * mm, "end": v(106.67, 2014) * mm});
            skArc(sketch, "E113.MirrorCS", {"start": v(246.67, 2022) * mm, "mid": v(247.25, 2023.41) * mm, "end": v(248.67, 2024) * mm});
            skLineSegment(sketch, "E114.MirrorCS", {"start": v(280, 2014) * mm, "end": v(280, 2022) * mm});
            skArc(sketch, "E115.MirrorCS", {"start": v(92, 2012) * mm, "mid": v(90.59, 2012.59) * mm, "end": v(90, 2014) * mm});
            skArc(sketch, "E116.MirrorCS", {"start": v(304.67, 2024) * mm, "mid": v(306.08, 2023.41) * mm, "end": v(306.67, 2022) * mm});
            skLineSegment(sketch, "E117.MirrorCS", {"start": v(340, 2014) * mm, "end": v(340, 2022) * mm});
            skLineSegment(sketch, "E118.MirrorCS", {"start": v(342, 2012) * mm, "end": v(344.67, 2012) * mm});
            skLineSegment(sketch, "E119.MirrorCS", {"start": v(332, 2024) * mm, "end": v(338, 2024) * mm});
            skLineSegment(sketch, "E120.MirrorCS", {"start": v(296.67, 2014) * mm, "end": v(296.67, 2022) * mm});
            skLineSegment(sketch, "E121.MirrorCS", {"start": v(65.33, 2024) * mm, "end": v(71.33, 2024) * mm});
            skArc(sketch, "E122.MirrorCS", {"start": v(296.67, 2014) * mm, "mid": v(296.08, 2012.59) * mm, "end": v(294.67, 2012) * mm});
            skLineSegment(sketch, "E123.MirrorCS", {"start": v(290, 2014) * mm, "end": v(290, 2022) * mm});
            skLineSegment(sketch, "E124.MirrorCS", {"start": v(90, 2014) * mm, "end": v(90, 2022) * mm});
            skArc(sketch, "E125.MirrorCS", {"start": v(258.67, 2012) * mm, "mid": v(257.25, 2012.59) * mm, "end": v(256.67, 2014) * mm});
            skLineSegment(sketch, "E126.MirrorCS", {"start": v(325.33, 2012) * mm, "end": v(328, 2012) * mm});
            skLineSegment(sketch, "E127.MirrorCS", {"start": v(73.33, 2014) * mm, "end": v(73.33, 2022) * mm});
            skArc(sketch, "E128.MirrorCS", {"start": v(288, 2024) * mm, "mid": v(289.41, 2023.41) * mm, "end": v(290, 2022) * mm});
            skArc(sketch, "E129.MirrorCS", {"start": v(263.33, 2022) * mm, "mid": v(263.92, 2023.41) * mm, "end": v(265.33, 2024) * mm});
            skArc(sketch, "E130.MirrorCS", {"start": v(275.33, 2012) * mm, "mid": v(273.92, 2012.59) * mm, "end": v(273.33, 2014) * mm});
            skArc(sketch, "E131.MirrorCS", {"start": v(88, 2024) * mm, "mid": v(89.41, 2023.41) * mm, "end": v(90, 2022) * mm});
            skLineSegment(sketch, "E132.MirrorCS", {"start": v(315.33, 2024) * mm, "end": v(321.33, 2024) * mm});
            skArc(sketch, "E133.MirrorCS", {"start": v(280, 2022) * mm, "mid": v(280.59, 2023.41) * mm, "end": v(282, 2024) * mm});
            skArc(sketch, "E134.MirrorCS", {"start": v(80, 2014) * mm, "mid": v(79.41, 2012.59) * mm, "end": v(78, 2012) * mm});
            skArc(sketch, "E135.MirrorCS", {"start": v(80, 2022) * mm, "mid": v(80.59, 2023.41) * mm, "end": v(82, 2024) * mm});
            skLineSegment(sketch, "E136.MirrorCS", {"start": v(313.33, 2014) * mm, "end": v(313.33, 2022) * mm});
            skArc(sketch, "E137.MirrorCS", {"start": v(313.33, 2014) * mm, "mid": v(312.75, 2012.59) * mm, "end": v(311.33, 2012) * mm});
            skLineSegment(sketch, "E138.MirrorCS", {"start": v(42, 2012) * mm, "end": v(44.67, 2012) * mm});
            skLineSegment(sketch, "E139.MirrorCS", {"start": v(63.33, 2014) * mm, "end": v(63.33, 2022) * mm});
            skLineSegment(sketch, "E140.MirrorCS", {"start": v(330, 2014) * mm, "end": v(330, 2022) * mm});
            skArc(sketch, "E141.MirrorCS", {"start": v(330, 2014) * mm, "mid": v(329.41, 2012.59) * mm, "end": v(328, 2012) * mm});
            skLineSegment(sketch, "E142.MirrorCS", {"start": v(323.33, 2014) * mm, "end": v(323.33, 2022) * mm});
            skArc(sketch, "E143.MirrorCS", {"start": v(296.67, 2022) * mm, "mid": v(297.25, 2023.41) * mm, "end": v(298.67, 2024) * mm});
            skLineSegment(sketch, "E144.MirrorCS", {"start": v(58.67, 2012) * mm, "end": v(61.33, 2012) * mm});
            skArc(sketch, "E145.MirrorCS", {"start": v(321.33, 2024) * mm, "mid": v(322.75, 2023.41) * mm, "end": v(323.33, 2022) * mm});
            skArc(sketch, "E146.MirrorCS", {"start": v(71.33, 2024) * mm, "mid": v(72.75, 2023.41) * mm, "end": v(73.33, 2022) * mm});
            skArc(sketch, "E147.MirrorCS", {"start": v(338, 2024) * mm, "mid": v(339.41, 2023.41) * mm, "end": v(340, 2022) * mm});
            skArc(sketch, "E148.MirrorCS", {"start": v(308.67, 2012) * mm, "mid": v(307.25, 2012.59) * mm, "end": v(306.67, 2014) * mm});
            skArc(sketch, "E149.MirrorCS", {"start": v(292, 2012) * mm, "mid": v(290.59, 2012.59) * mm, "end": v(290, 2014) * mm});
            skArc(sketch, "E150.MirrorCS", {"start": v(346.67, 2014) * mm, "mid": v(346.08, 2012.59) * mm, "end": v(344.67, 2012) * mm});
            skArc(sketch, "E151.MirrorCS", {"start": v(75.33, 2012) * mm, "mid": v(73.92, 2012.59) * mm, "end": v(73.33, 2014) * mm});
            skArc(sketch, "E152.MirrorCS", {"start": v(313.33, 2022) * mm, "mid": v(313.92, 2023.41) * mm, "end": v(315.33, 2024) * mm});
            skLineSegment(sketch, "E153.MirrorCS", {"start": v(346.67, 2014) * mm, "end": v(346.67, 2022) * mm});
            skArc(sketch, "E154.MirrorCS", {"start": v(330, 2022) * mm, "mid": v(330.59, 2023.41) * mm, "end": v(332, 2024) * mm});
            skLineSegment(sketch, "E155.MirrorCS", {"start": v(365.33, 2024) * mm, "end": v(371.33, 2024) * mm});
            skLineSegment(sketch, "E156.MirrorCS", {"start": v(15.83, 2001.17) * mm, "end": v(20.83, 2001.17) * mm, "construction": true});
            skArc(sketch, "E157.MirrorCS", {"start": v(325.33, 2012) * mm, "mid": v(323.92, 2012.59) * mm, "end": v(323.33, 2014) * mm});
            skLineSegment(sketch, "E158.MirrorCS", {"start": v(15.83, 2006.17) * mm, "end": v(20.83, 2006.17) * mm, "construction": true});
            skArc(sketch, "E159.MirrorCS", {"start": v(63.33, 2014) * mm, "mid": v(62.75, 2012.59) * mm, "end": v(61.33, 2012) * mm});
            skArc(sketch, "E160.MirrorCS", {"start": v(38, 2024) * mm, "mid": v(39.41, 2023.41) * mm, "end": v(40, 2022) * mm});
            skLineSegment(sketch, "E161.MirrorCS", {"start": v(348.67, 2024) * mm, "end": v(354.67, 2024) * mm});
            skLineSegment(sketch, "E162.MirrorCS", {"start": v(48.67, 2024) * mm, "end": v(54.67, 2024) * mm});
            skArc(sketch, "E163.MirrorCS", {"start": v(63.33, 2022) * mm, "mid": v(63.92, 2023.41) * mm, "end": v(65.33, 2024) * mm});
            skLineSegment(sketch, "E164.MirrorCS", {"start": v(40, 2014) * mm, "end": v(40, 2022) * mm});
            skArc(sketch, "E165.MirrorCS", {"start": v(342, 2012) * mm, "mid": v(340.59, 2012.59) * mm, "end": v(340, 2014) * mm});
            skArc(sketch, "E166.MirrorCS", {"start": v(346.67, 2022) * mm, "mid": v(347.25, 2023.41) * mm, "end": v(348.67, 2024) * mm});
            skArc(sketch, "E167.MirrorCS", {"start": v(46.67, 2014) * mm, "mid": v(46.08, 2012.59) * mm, "end": v(44.67, 2012) * mm});
            skLineSegment(sketch, "E168.MirrorCS", {"start": v(46.67, 2014) * mm, "end": v(46.67, 2022) * mm});
            skLineSegment(sketch, "E169.MirrorCS", {"start": v(15.83, 2001.17) * mm, "end": v(15.83, 2006.17) * mm, "construction": true});
            skLineSegment(sketch, "E170.MirrorCS", {"start": v(30, 2014) * mm, "end": v(30, 2022) * mm});
            skLineSegment(sketch, "E171.MirrorCS", {"start": v(375.33, 2012) * mm, "end": v(378, 2012) * mm});
            skLineSegment(sketch, "E172.MirrorCS", {"start": v(356.67, 2014) * mm, "end": v(356.67, 2022) * mm});
            skLineSegment(sketch, "E173.MirrorCS", {"start": v(32, 2024) * mm, "end": v(38, 2024) * mm});
            skLineSegment(sketch, "E174.MirrorCS", {"start": v(358.67, 2012) * mm, "end": v(361.33, 2012) * mm});
            skLineSegment(sketch, "E175.MirrorCS", {"start": v(56.67, 2014) * mm, "end": v(56.67, 2022) * mm});
            skArc(sketch, "E176.MirrorCS", {"start": v(58.67, 2012) * mm, "mid": v(57.25, 2012.59) * mm, "end": v(56.67, 2014) * mm});
            skArc(sketch, "E177.MirrorCS", {"start": v(354.67, 2024) * mm, "mid": v(356.08, 2023.41) * mm, "end": v(356.67, 2022) * mm});
            skArc(sketch, "E178.MirrorCS", {"start": v(54.67, 2024) * mm, "mid": v(56.08, 2023.41) * mm, "end": v(56.67, 2022) * mm});
            skLineSegment(sketch, "E179.MirrorCS", {"start": v(373.33, 2014) * mm, "end": v(373.33, 2022) * mm});
            skArc(sketch, "E180.MirrorCS", {"start": v(371.33, 2024) * mm, "mid": v(372.75, 2023.41) * mm, "end": v(373.33, 2022) * mm});
            skArc(sketch, "E181.MirrorCS", {"start": v(42, 2012) * mm, "mid": v(40.59, 2012.59) * mm, "end": v(40, 2014) * mm});
            skArc(sketch, "E182.MirrorCS", {"start": v(46.67, 2022) * mm, "mid": v(47.25, 2023.41) * mm, "end": v(48.67, 2024) * mm});
            skLineSegment(sketch, "E183.MirrorCS", {"start": v(380, 2014) * mm, "end": v(380, 2022) * mm});
            skArc(sketch, "E184.MirrorCS", {"start": v(363.33, 2022) * mm, "mid": v(363.92, 2023.41) * mm, "end": v(365.33, 2024) * mm});
            skLineSegment(sketch, "E185.MirrorCS", {"start": v(363.33, 2014) * mm, "end": v(363.33, 2022) * mm});
            skLineSegment(sketch, "E186.MirrorCS", {"start": v(25.33, 2012) * mm, "end": v(28, 2012) * mm});
            skLineSegment(sketch, "E187.MirrorCS", {"start": v(20.83, 2001.17) * mm, "end": v(20.83, 2006.17) * mm, "construction": true});
            skArc(sketch, "E188.MirrorCS", {"start": v(25.33, 2012) * mm, "mid": v(23.92, 2012.59) * mm, "end": v(23.33, 2014) * mm});
            skArc(sketch, "E189.MirrorCS", {"start": v(30, 2022) * mm, "mid": v(30.59, 2023.41) * mm, "end": v(32, 2024) * mm});
            skArc(sketch, "E190.MirrorCS", {"start": v(363.33, 2014) * mm, "mid": v(362.75, 2012.59) * mm, "end": v(361.33, 2012) * mm});
            skLineSegment(sketch, "E191.MirrorCS", {"start": v(382, 2024) * mm, "end": v(388, 2024) * mm});
            skArc(sketch, "E192.MirrorCS", {"start": v(380, 2022) * mm, "mid": v(380.59, 2023.41) * mm, "end": v(382, 2024) * mm});
            skArc(sketch, "E193.MirrorCS", {"start": v(375.33, 2012) * mm, "mid": v(373.92, 2012.59) * mm, "end": v(373.33, 2014) * mm});
            skArc(sketch, "E194.MirrorCS", {"start": v(358.67, 2012) * mm, "mid": v(357.25, 2012.59) * mm, "end": v(356.67, 2014) * mm});
            skArc(sketch, "E195.MirrorCS", {"start": v(380, 2014) * mm, "mid": v(379.41, 2012.59) * mm, "end": v(378, 2012) * mm});
            skArc(sketch, "E196.MirrorCS", {"start": v(21.33, 2024) * mm, "mid": v(22.75, 2023.41) * mm, "end": v(23.33, 2022) * mm});
            skArc(sketch, "E197.MirrorCS", {"start": v(30, 2014) * mm, "mid": v(29.41, 2012.59) * mm, "end": v(28, 2012) * mm});
            skLineSegment(sketch, "E198.MirrorCS", {"start": v(18.33, 2006.17) * mm, "end": v(18.33, 2001.17) * mm, "construction": true});
            skLineSegment(sketch, "E199.MirrorCS", {"start": v(21.33, 2024) * mm, "end": v(38, 2024) * mm, "construction": true});
            skLineSegment(sketch, "E200.MirrorCS", {"start": v(23.33, 2014) * mm, "end": v(23.33, 2022) * mm});
            skLineSegment(sketch, "E201.MirrorCS", {"start": v(390, 2014) * mm, "end": v(390, 2022) * mm});
            skLineSegment(sketch, "E202.MirrorCS", {"start": v(392, 2012) * mm, "end": v(394.67, 2012) * mm});
            skLineSegment(sketch, "E203.MirrorCS", {"start": v(10, 2024) * mm, "end": v(10, 1995.28) * mm, "construction": true});
            skLineSegment(sketch, "E204.MirrorCS", {"start": v(15.83, 2003.67) * mm, "end": v(20.83, 2003.67) * mm, "construction": true});
            skLineSegment(sketch, "E205.MirrorCS", {"start": v(398.67, 2024) * mm, "end": v(404.67, 2024) * mm});
            skArc(sketch, "E206.MirrorCS", {"start": v(388, 2024) * mm, "mid": v(389.41, 2023.41) * mm, "end": v(390, 2022) * mm});
            skArc(sketch, "E207.MirrorCS", {"start": v(392, 2012) * mm, "mid": v(390.59, 2012.59) * mm, "end": v(390, 2014) * mm});
            skArc(sketch, "E208.MirrorCS", {"start": v(396.67, 2022) * mm, "mid": v(397.25, 2023.41) * mm, "end": v(398.67, 2024) * mm});
            skLineSegment(sketch, "E209.MirrorCS", {"start": v(396.67, 2014) * mm, "end": v(396.67, 2022) * mm});
            skArc(sketch, "E210.MirrorCS", {"start": v(396.67, 2014) * mm, "mid": v(396.08, 2012.59) * mm, "end": v(394.67, 2012) * mm});
            skLineSegment(sketch, "E211.MirrorCS", {"start": v(404.67, 2024) * mm, "end": v(408.26, 2022.51) * mm});
            skLineSegment(sketch, "E212.MirrorCS", {"start": v(2, 2024) * mm, "end": v(21.33, 2024) * mm});
            skPoint(sketch, "E213.MirrorP", {"position": v(256.67, 2024) * mm});
            skPoint(sketch, "E214.MirrorP", {"position": v(130, 2012) * mm});
            skPoint(sketch, "E215.MirrorP", {"position": v(90, 2024) * mm});
            skPoint(sketch, "E216.MirrorP", {"position": v(196.67, 2012) * mm});
            skPoint(sketch, "E217.MirrorP", {"position": v(123.33, 2024) * mm});
            skPoint(sketch, "E218.MirrorP", {"position": v(190, 2024) * mm});
            skPoint(sketch, "E219.MirrorP", {"position": v(56.67, 2024) * mm});
            skPoint(sketch, "E220.MirrorP", {"position": v(330, 2012) * mm});
            skPoint(sketch, "E221.MirrorP", {"position": v(263.33, 2012) * mm});
            skPoint(sketch, "E222.MirrorP", {"position": v(63.33, 2012) * mm});
            skPoint(sketch, "E223.MirrorP", {"position": v(290, 2024) * mm});
            skPoint(sketch, "E224.MirrorP", {"position": v(363.33, 2012) * mm});
            skPoint(sketch, "E225.MirrorP", {"position": v(296.67, 2012) * mm});
            skPoint(sketch, "E226.MirrorP", {"position": v(163.33, 2012) * mm});
            skPoint(sketch, "E227.MirrorP", {"position": v(156.67, 2024) * mm});
            skPoint(sketch, "E228.MirrorP", {"position": v(223.33, 2024) * mm});
            skPoint(sketch, "E229.MirrorP", {"position": v(230, 2012) * mm});
            skPoint(sketch, "E230.MirrorP", {"position": v(323.33, 2024) * mm});
            skPoint(sketch, "E231.MirrorP", {"position": v(96.67, 2012) * mm});
            skPoint(sketch, "E232.MirrorP", {"position": v(273.33, 2012) * mm});
            skPoint(sketch, "E233.MirrorP", {"position": v(140, 2012) * mm});
            skPoint(sketch, "E234.MirrorP", {"position": v(40, 2012) * mm});
            skPoint(sketch, "E235.MirrorP", {"position": v(246.67, 2024) * mm});
            skPoint(sketch, "E236.MirrorP", {"position": v(113.33, 2024) * mm});
            skPoint(sketch, "E237.MirrorP", {"position": v(280, 2024) * mm});
            skPoint(sketch, "E238.MirrorP", {"position": v(46.67, 2024) * mm});
            skPoint(sketch, "E239.MirrorP", {"position": v(146.67, 2024) * mm});
            skPoint(sketch, "E240.MirrorP", {"position": v(356.67, 2024) * mm});
            skPoint(sketch, "E241.MirrorP", {"position": v(23.33, 2012) * mm});
            skPoint(sketch, "E242.MirrorP", {"position": v(30, 2024) * mm});
            skPoint(sketch, "E243.MirrorP", {"position": v(313.33, 2012) * mm});
            skPoint(sketch, "E244.MirrorP", {"position": v(180, 2012) * mm});
            skPoint(sketch, "E245.MirrorP", {"position": v(46.67, 2012) * mm});
            skPoint(sketch, "E246.MirrorP", {"position": v(23.33, 2024) * mm});
            skPoint(sketch, "E247.MirrorP", {"position": v(273.33, 2024) * mm});
            skPoint(sketch, "E248.MirrorP", {"position": v(140, 2024) * mm});
            skPoint(sketch, "E249.MirrorP", {"position": v(40, 2024) * mm});
            skPoint(sketch, "E250.MirrorP", {"position": v(306.67, 2012) * mm});
            skPoint(sketch, "E251.MirrorP", {"position": v(340, 2012) * mm});
            skPoint(sketch, "E252.MirrorP", {"position": v(173.33, 2012) * mm});
            skPoint(sketch, "E253.MirrorP", {"position": v(373.33, 2012) * mm});
            skPoint(sketch, "E254.MirrorP", {"position": v(206.67, 2012) * mm});
            skPoint(sketch, "E255.MirrorP", {"position": v(240, 2012) * mm});
            skPoint(sketch, "E256.MirrorP", {"position": v(106.67, 2012) * mm});
            skPoint(sketch, "E257.MirrorP", {"position": v(73.33, 2012) * mm});
            skPoint(sketch, "E258.MirrorP", {"position": v(313.33, 2024) * mm});
            skPoint(sketch, "E259.MirrorP", {"position": v(346.67, 2024) * mm});
            skPoint(sketch, "E260.MirrorP", {"position": v(213.33, 2024) * mm});
            skPoint(sketch, "E261.MirrorP", {"position": v(180, 2024) * mm});
            skPoint(sketch, "E262.MirrorP", {"position": v(80, 2024) * mm});
            skPoint(sketch, "E263.MirrorP", {"position": v(323.33, 2012) * mm});
            skPoint(sketch, "E264.MirrorP", {"position": v(190, 2012) * mm});
            skPoint(sketch, "E265.MirrorP", {"position": v(56.67, 2012) * mm});
            skPoint(sketch, "E266.MirrorP", {"position": v(390, 2024) * mm});
            skPoint(sketch, "E267.MirrorP", {"position": v(346.67, 2012) * mm});
            skPoint(sketch, "E268.MirrorP", {"position": v(380, 2012) * mm});
            skPoint(sketch, "E269.MirrorP", {"position": v(246.67, 2012) * mm});
            skPoint(sketch, "E270.MirrorP", {"position": v(213.33, 2012) * mm});
            skPoint(sketch, "E271.MirrorP", {"position": v(280, 2012) * mm});
            skPoint(sketch, "E272.MirrorP", {"position": v(196.67, 2024) * mm});
            skPoint(sketch, "E273.MirrorP", {"position": v(113.33, 2012) * mm});
            skPoint(sketch, "E274.MirrorP", {"position": v(30, 2012) * mm});
            skPoint(sketch, "E275.MirrorP", {"position": v(146.67, 2012) * mm});
            skPoint(sketch, "E276.MirrorP", {"position": v(80, 2012) * mm});
            skPoint(sketch, "E277.MirrorP", {"position": v(0, 2012) * mm});
            skPoint(sketch, "E278.MirrorP", {"position": v(373.33, 2024) * mm});
            skPoint(sketch, "E279.MirrorP", {"position": v(173.33, 2024) * mm});
            skPoint(sketch, "E280.MirrorP", {"position": v(206.67, 2024) * mm});
            skPoint(sketch, "E281.MirrorP", {"position": v(240, 2024) * mm});
            skPoint(sketch, "E282.MirrorP", {"position": v(73.33, 2024) * mm});
            skPoint(sketch, "E283.MirrorP", {"position": v(106.67, 2024) * mm});
            skPoint(sketch, "E284.MirrorP", {"position": v(63.33, 2024) * mm});
            skPoint(sketch, "E285.MirrorP", {"position": v(306.67, 2024) * mm});
            skPoint(sketch, "E286.MirrorP", {"position": v(340, 2024) * mm});
            skPoint(sketch, "E287.MirrorP", {"position": v(380, 2024) * mm});
            skPoint(sketch, "E288.MirrorP", {"position": v(123.33, 2012) * mm});
            skPoint(sketch, "E289.MirrorP", {"position": v(156.67, 2012) * mm});
            skPoint(sketch, "E290.MirrorP", {"position": v(396.67, 2024) * mm});
            skPoint(sketch, "E291.MirrorP", {"position": v(363.33, 2024) * mm});
            skPoint(sketch, "E292.MirrorP", {"position": v(90, 2012) * mm});
            skPoint(sketch, "E293.MirrorP", {"position": v(230, 2024) * mm});
            skPoint(sketch, "E294.MirrorP", {"position": v(263.33, 2024) * mm});
            skPoint(sketch, "E295.MirrorP", {"position": v(96.67, 2024) * mm});
            skPoint(sketch, "E296.MirrorP", {"position": v(130, 2024) * mm});
            skPoint(sketch, "E297.MirrorP", {"position": v(163.33, 2024) * mm});
            skPoint(sketch, "E298.MirrorP", {"position": v(396.67, 2012) * mm});
            skPoint(sketch, "E299.MirrorP", {"position": v(223.33, 2012) * mm});
            skPoint(sketch, "E300.MirrorP", {"position": v(290, 2012) * mm});
            skPoint(sketch, "E301.MirrorP", {"position": v(296.67, 2024) * mm});
            skPoint(sketch, "E302.MirrorP", {"position": v(330, 2024) * mm});
            skPoint(sketch, "E303.MirrorP", {"position": v(256.67, 2012) * mm});
            skPoint(sketch, "E304.MirrorP", {"position": v(356.67, 2012) * mm});
            skPoint(sketch, "E305.MirrorP", {"position": v(390, 2012) * mm});
            skPoint(sketch, "E306.visualSharp", {"position": v(409.5, 2022) * mm});
            skArc(sketch, "E306.filletArc", {"start": v(409.5, 2020.66) * mm, "mid": v(409.16, 2021.77) * mm, "end": v(408.26, 2022.51) * mm});
            skPoint(sketch, "E307.visualSharp", {"position": v(0, 2024) * mm});
            skArc(sketch, "E307.filletArc", {"start": v(2, 2024) * mm, "mid": v(0.59, 2023.41) * mm, "end": v(0, 2022) * mm});
            skPoint(sketch, "E308.visualSharp", {"position": v(0, 0) * mm});
            skArc(sketch, "E308.filletArc", {"start": v(0, 2) * mm, "mid": v(0.59, 0.59) * mm, "end": v(2, 0) * mm});
            skPoint(sketch, "E309.visualSharp", {"position": v(409.5, 2) * mm});
            skArc(sketch, "E309.filletArc", {"start": v(408.26, 1.49) * mm, "mid": v(409.16, 2.23) * mm, "end": v(409.5, 3.34) * mm});
            skLineSegment(sketch, "E310.1.0.0", {"start": v(30, 12) * mm, "end": v(30, 2020) * mm, "construction": true});
            skLineSegment(sketch, "E310.1.0.1", {"start": v(40, 12) * mm, "end": v(40, 2020) * mm, "construction": true});
            skLineSegment(sketch, "E310.2.0.0", {"start": v(46.67, 12) * mm, "end": v(46.67, 2020) * mm, "construction": true});
            skLineSegment(sketch, "E310.2.0.1", {"start": v(56.67, 12) * mm, "end": v(56.67, 2020) * mm, "construction": true});
            skLineSegment(sketch, "E310.3.0.0", {"start": v(63.33, 12) * mm, "end": v(63.33, 2020) * mm, "construction": true});
            skLineSegment(sketch, "E310.3.0.1", {"start": v(73.33, 12) * mm, "end": v(73.33, 2020) * mm, "construction": true});
            skLineSegment(sketch, "E310.4.0.0", {"start": v(80, 12) * mm, "end": v(80, 2020) * mm, "construction": true});
            skLineSegment(sketch, "E310.4.0.1", {"start": v(90, 12) * mm, "end": v(90, 2020) * mm, "construction": true});
            skLineSegment(sketch, "E310.5.0.0", {"start": v(96.67, 12) * mm, "end": v(96.67, 2020) * mm, "construction": true});
            skLineSegment(sketch, "E310.5.0.1", {"start": v(106.67, 12) * mm, "end": v(106.67, 2020) * mm, "construction": true});
            skLineSegment(sketch, "E310.6.0.0", {"start": v(113.33, 12) * mm, "end": v(113.33, 2020) * mm, "construction": true});
            skLineSegment(sketch, "E310.6.0.1", {"start": v(123.33, 12) * mm, "end": v(123.33, 2020) * mm, "construction": true});
            skLineSegment(sketch, "E310.7.0.0", {"start": v(130, 12) * mm, "end": v(130, 2020) * mm, "construction": true});
            skLineSegment(sketch, "E310.7.0.1", {"start": v(140, 12) * mm, "end": v(140, 2020) * mm, "construction": true});
            skLineSegment(sketch, "E310.8.0.0", {"start": v(146.67, 12) * mm, "end": v(146.67, 2020) * mm, "construction": true});
            skLineSegment(sketch, "E310.8.0.1", {"start": v(156.67, 12) * mm, "end": v(156.67, 2020) * mm, "construction": true});
            skLineSegment(sketch, "E310.9.0.0", {"start": v(163.33, 12) * mm, "end": v(163.33, 2020) * mm, "construction": true});
            skLineSegment(sketch, "E310.9.0.1", {"start": v(173.33, 12) * mm, "end": v(173.33, 2020) * mm, "construction": true});
            skLineSegment(sketch, "E310.10.0.0", {"start": v(180, 12) * mm, "end": v(180, 2020) * mm, "construction": true});
            skLineSegment(sketch, "E310.10.0.1", {"start": v(190, 12) * mm, "end": v(190, 2020) * mm, "construction": true});
            skLineSegment(sketch, "E310.11.0.0", {"start": v(196.67, 12) * mm, "end": v(196.67, 2020) * mm, "construction": true});
            skLineSegment(sketch, "E310.11.0.1", {"start": v(206.67, 12) * mm, "end": v(206.67, 2020) * mm, "construction": true});
            skLineSegment(sketch, "E310.direction1", {"start": v(13.33, 12) * mm, "end": v(30, 12) * mm, "construction": true});
            skSolve(sketch);
        }
        {
            var Q0;
            Q0=qCreatedBy(makeId("Top.planeOp"),FACE);
            var sketch = newSketch(context, id + "F1", { "sketchPlane" : qUnion([Q0])});
            skCircle(sketch, "E311", {"center": v(95.5, 178.44) * mm, "radius": 73 * mm});
            skCircle(sketch, "E312", {"center": v(95.5, 178.44) * mm, "radius": 40 * mm});
            skLineSegment(sketch, "E313", {"start": v(95.5, 178.44) * mm, "end": v(95.5, 97.69) * mm, "construction": true});
            skCircle(sketch, "E314", {"center": v(95.5, 97.69) * mm, "radius": 2.25 * mm});
            skLineSegment(sketch, "E315", {"start": v(95.5, 178.44) * mm, "end": v(147.9, 178.44) * mm, "construction": true});
            skCircle(sketch, "E316.MirrorC", {"center": v(95.5, 259.19) * mm, "radius": 2.25 * mm});
            skCircle(sketch, "E317", {"center": v(162.5, 223.5) * mm, "radius": 2.25 * mm});
            skCircle(sketch, "E318.MirrorC", {"center": v(28.5, 223.5) * mm, "radius": 2.25 * mm});
            skCircle(sketch, "E319", {"center": v(95.5, 178.44) * mm, "radius": 31 * mm});
            skCircle(sketch, "E320", {"center": v(95.5, 178.44) * mm, "radius": 57.75 * mm});
            skLineSegment(sketch, "E321", {"start": v(147.9, 230.84) * mm, "end": v(147.9, 126.04) * mm, "construction": true});
            skCircle(sketch, "E322", {"center": v(95.5, 178.44) * mm, "radius": 74.1 * mm, "construction": true});
            skCircle(sketch, "E323", {"center": v(145.16, 233.44) * mm, "radius": 2.15 * mm});
            skCircle(sketch, "E324.1.0", {"center": v(40.5, 228.1) * mm, "radius": 2.15 * mm});
            skCircle(sketch, "E324.2.0", {"center": v(45.84, 123.44) * mm, "radius": 2.15 * mm});
            skCircle(sketch, "E324.3.0", {"center": v(150.5, 128.77) * mm, "radius": 2.15 * mm});
            skSolve(sketch);
        }
        {
            var Q0;
            Q0=qCreatedBy(makeId("Top.planeOp"),FACE);
            var sketch = newSketch(context, id + "F2", { "sketchPlane" : qUnion([Q0])});
            skArc(sketch, "E325.0", {"start": v(80.08, 249.79) * mm, "mid": v(76.78, 249) * mm, "end": v(73.5, 248.04) * mm});
            skLineSegment(sketch, "E326.trimOffspring", {"start": v(25.33, 158.3) * mm, "end": v(25.33, 198.58) * mm});
            skLineSegment(sketch, "E327.trimOffspring", {"start": v(32, 142.43) * mm, "end": v(32, 214.45) * mm});
            skLineSegment(sketch, "E328.trimOffspring", {"start": v(42, 128.77) * mm, "end": v(42, 228.1) * mm});
            skLineSegment(sketch, "E329.trimOffspring", {"start": v(48.67, 122.44) * mm, "end": v(48.67, 234.43) * mm});
            skLineSegment(sketch, "E330.trimOffspring", {"start": v(58.67, 115.4) * mm, "end": v(58.67, 194.03) * mm});
            skLineSegment(sketch, "E331.trimOffspring", {"start": v(65.33, 111.96) * mm, "end": v(65.33, 204.7) * mm});
            skLineSegment(sketch, "E332.trimOffspring", {"start": v(75.33, 108.28) * mm, "end": v(74.87, 143.62) * mm});
            skLineSegment(sketch, "E333.trimOffspring", {"start": v(82, 106.7) * mm, "end": v(81.55, 140.6) * mm});
            skLineSegment(sketch, "E334.trimOffspring", {"start": v(92, 105.52) * mm, "end": v(92, 138.59) * mm});
            skLineSegment(sketch, "E335.trimOffspring", {"start": v(98.67, 105.5) * mm, "end": v(98.67, 138.56) * mm});
            skLineSegment(sketch, "E336.trimOffspring", {"start": v(108.67, 106.63) * mm, "end": v(108.67, 140.66) * mm});
            skLineSegment(sketch, "E337.trimOffspring", {"start": v(115.33, 108.18) * mm, "end": v(115.33, 143.7) * mm});
            skLineSegment(sketch, "E338.trimOffspring", {"start": v(125.33, 111.81) * mm, "end": v(125.33, 151.8) * mm});
            skLineSegment(sketch, "E339.trimOffspring", {"start": v(132, 115.22) * mm, "end": v(132, 162.07) * mm});
            skLineSegment(sketch, "E340.trimOffspring", {"start": v(142, 122.16) * mm, "end": v(142, 234.7) * mm});
            skLineSegment(sketch, "E341.trimOffspring", {"start": v(148.67, 128.41) * mm, "end": v(148.67, 228.46) * mm});
            skLineSegment(sketch, "E342.trimOffspring", {"start": v(158.67, 141.84) * mm, "end": v(158.67, 215.03) * mm});
            skLineSegment(sketch, "E343.trimOffspring", {"start": v(165.16, 156.6) * mm, "end": v(165.16, 200.27) * mm});
            skArc(sketch, "E344", {"start": v(102.09, 100.71) * mm, "mid": v(173.5, 178.44) * mm, "end": v(102.09, 256.16) * mm});
            skLineSegment(sketch, "E345.trimOffspring", {"start": v(132, 162.07) * mm, "end": v(132, 241.66) * mm});
            skLineSegment(sketch, "E346.trimOffspring", {"start": v(125.33, 151.8) * mm, "end": v(125.33, 245.06) * mm});
            skLineSegment(sketch, "E347.trimOffspring", {"start": v(115.33, 143.7) * mm, "end": v(115.33, 248.69) * mm});
            skLineSegment(sketch, "E348.trimOffspring", {"start": v(108.67, 140.66) * mm, "end": v(108.67, 250.24) * mm});
            skLineSegment(sketch, "E349.trimOffspring", {"start": v(98.67, 138.56) * mm, "end": v(98.67, 251.37) * mm});
            skLineSegment(sketch, "E350.trimOffspring", {"start": v(92, 138.59) * mm, "end": v(92, 251.35) * mm});
            skLineSegment(sketch, "E351.trimOffspring", {"start": v(81.55, 140.6) * mm, "end": v(80.08, 249.79) * mm});
            skLineSegment(sketch, "E352.trimOffspring", {"start": v(74.87, 143.62) * mm, "end": v(73.5, 248.04) * mm});
            skLineSegment(sketch, "E353.trimOffspring", {"start": v(65.33, 204.7) * mm, "end": v(65.33, 244.91) * mm});
            skLineSegment(sketch, "E354.trimOffspring", {"start": v(58.67, 194.03) * mm, "end": v(58.67, 241.46) * mm});
            skCircle(sketch, "E355.0", {"center": v(95.5, 259.19) * mm, "radius": 2.25 * mm});
            skCircle(sketch, "E356.0", {"center": v(95.5, 97.69) * mm, "radius": 2.25 * mm});
            skArc(sketch, "E357.trimOffspring", {"start": v(98.67, 251.37) * mm, "mid": v(95.33, 251.44) * mm, "end": v(92, 251.35) * mm});
            skArc(sketch, "E358.trimOffspring", {"start": v(115.33, 248.69) * mm, "mid": v(112.02, 249.54) * mm, "end": v(108.67, 250.24) * mm});
            skArc(sketch, "E359.trimOffspring", {"start": v(132, 241.66) * mm, "mid": v(128.71, 243.44) * mm, "end": v(125.33, 245.06) * mm});
            skArc(sketch, "E360.trimOffspring", {"start": v(148.67, 228.46) * mm, "mid": v(145.43, 231.69) * mm, "end": v(142, 234.7) * mm});
            skArc(sketch, "E361.trimOffspring", {"start": v(158.67, 141.84) * mm, "mid": v(162.32, 149.04) * mm, "end": v(165.16, 156.6) * mm});
            skArc(sketch, "E362.trimOffspring", {"start": v(165.16, 200.27) * mm, "mid": v(162.32, 207.83) * mm, "end": v(158.67, 215.03) * mm});
            skArc(sketch, "E363.trimOffspring", {"start": v(142, 122.16) * mm, "mid": v(145.43, 125.18) * mm, "end": v(148.67, 128.41) * mm});
            skArc(sketch, "E364.trimOffspring", {"start": v(125.33, 111.81) * mm, "mid": v(128.71, 113.43) * mm, "end": v(132, 115.22) * mm});
            skArc(sketch, "E365.trimOffspring", {"start": v(108.67, 106.63) * mm, "mid": v(112.02, 107.33) * mm, "end": v(115.33, 108.18) * mm});
            skArc(sketch, "E366.trimOffspring", {"start": v(92, 105.52) * mm, "mid": v(95.33, 105.44) * mm, "end": v(98.67, 105.5) * mm});
            skArc(sketch, "E367.trimOffspring", {"start": v(75.33, 108.28) * mm, "mid": v(78.65, 107.4) * mm, "end": v(82, 106.7) * mm});
            skArc(sketch, "E368.trimOffspring", {"start": v(58.67, 115.4) * mm, "mid": v(61.96, 113.6) * mm, "end": v(65.33, 111.96) * mm});
            skArc(sketch, "E369.trimOffspring", {"start": v(42, 128.77) * mm, "mid": v(45.23, 125.5) * mm, "end": v(48.67, 122.44) * mm});
            skArc(sketch, "E370.trimOffspring", {"start": v(25.33, 158.3) * mm, "mid": v(28.2, 150.16) * mm, "end": v(32, 142.43) * mm});
            skArc(sketch, "E371.trimOffspring", {"start": v(32, 214.45) * mm, "mid": v(28.2, 206.7) * mm, "end": v(25.33, 198.58) * mm});
            skArc(sketch, "E372.trimOffspring", {"start": v(48.67, 234.43) * mm, "mid": v(45.23, 231.37) * mm, "end": v(42, 228.1) * mm});
            skArc(sketch, "E373.trimOffspring", {"start": v(65.33, 244.91) * mm, "mid": v(61.96, 243.27) * mm, "end": v(58.67, 241.46) * mm});
            skArc(sketch, "E374.0", {"start": v(88.91, 256.16) * mm, "mid": v(95.5, 266.44) * mm, "end": v(102.09, 256.16) * mm});
            skArc(sketch, "E375.0", {"start": v(88.91, 100.71) * mm, "mid": v(95.5, 90.44) * mm, "end": v(102.09, 100.71) * mm});
            skArc(sketch, "E376.trimOffspring", {"start": v(88.91, 256.16) * mm, "mid": v(17.5, 178.44) * mm, "end": v(88.91, 100.71) * mm});
            skSolve(sketch);
        }
        {
            var Q0;
            Q0 = qSketchRegion(id + "F2", true);
            extrude(context, id + "F3", {"entities" : qUnion([Q0]), "depth" : 2 * mm});
        }
        {
            var Q0;
            Q0=qCreatedBy(makeId("Top.planeOp"),FACE);
            var sketch = newSketch(context, id + "F4", { "sketchPlane" : qUnion([Q0])});
            skPoint(sketch, "E377.0", {"position": v(95.5, 178.44) * mm});
            skCircle(sketch, "E378.0", {"center": v(145.16, 233.44) * mm, "radius": 2.15 * mm});
            skCircle(sketch, "E379.0", {"center": v(45.84, 123.44) * mm, "radius": 2.15 * mm});
            skArc(sketch, "E380", {"start": v(57.23, 129.02) * mm, "mid": v(137.41, 224.8) * mm, "end": v(50.2, 135.39) * mm});
            skArc(sketch, "E381", {"start": v(148.66, 229.86) * mm, "mid": v(148.1, 237.49) * mm, "end": v(140.67, 235.63) * mm});
            skLineSegment(sketch, "E382", {"start": v(140.67, 235.63) * mm, "end": v(133.87, 227.77) * mm});
            skLineSegment(sketch, "E383", {"start": v(149.56, 231.05) * mm, "end": v(141.64, 220.59) * mm});
            skLineSegment(sketch, "E384.trimOffspring", {"start": v(148.67, 229.87) * mm, "end": v(148.67, 229.87) * mm});
            skLineSegment(sketch, "E385.trimOffspring", {"start": v(108.67, 234.66) * mm, "end": v(108.67, 122.2) * mm});
            skLineSegment(sketch, "E386.trimOffspring", {"start": v(125.33, 227.88) * mm, "end": v(125.33, 128.99) * mm});
            skLineSegment(sketch, "E387.trimOffspring", {"start": v(115.33, 232.67) * mm, "end": v(115.33, 124.2) * mm});
            skLineSegment(sketch, "E388.trimOffspring", {"start": v(148.67, 155.89) * mm, "end": v(148.67, 200.98) * mm});
            skLineSegment(sketch, "E389.trimOffspring", {"start": v(142, 144.19) * mm, "end": v(142, 212.68) * mm});
            skLineSegment(sketch, "E390.trimOffspring", {"start": v(132, 133.68) * mm, "end": v(132, 223.19) * mm});
            skLineSegment(sketch, "E391.trimOffspring", {"start": v(125.33, 128.99) * mm, "end": v(125.33, 227.88) * mm});
            skLineSegment(sketch, "E392.trimOffspring", {"start": v(115.33, 124.2) * mm, "end": v(115.33, 232.67) * mm});
            skLineSegment(sketch, "E393.trimOffspring", {"start": v(98.67, 120.77) * mm, "end": v(98.67, 236.1) * mm});
            skLineSegment(sketch, "E394.trimOffspring", {"start": v(92, 120.8) * mm, "end": v(92, 236.08) * mm});
            skLineSegment(sketch, "E395.trimOffspring", {"start": v(82, 122.29) * mm, "end": v(82, 234.59) * mm});
            skLineSegment(sketch, "E396.trimOffspring", {"start": v(75.33, 124.32) * mm, "end": v(75.33, 232.55) * mm});
            skLineSegment(sketch, "E397.trimOffspring", {"start": v(65.33, 129.2) * mm, "end": v(65.33, 227.68) * mm});
            skLineSegment(sketch, "E398.trimOffspring", {"start": v(58.67, 133.96) * mm, "end": v(58.67, 222.91) * mm});
            skLineSegment(sketch, "E399.trimOffspring", {"start": v(48.67, 144.65) * mm, "end": v(48.67, 212.22) * mm});
            skLineSegment(sketch, "E400.trimOffspring", {"start": v(42, 156.7) * mm, "end": v(42, 200.18) * mm});
            skArc(sketch, "E401", {"start": v(42.4, 127.06) * mm, "mid": v(42.54, 119.67) * mm, "end": v(49.89, 120.5) * mm});
            skLineSegment(sketch, "E402", {"start": v(42.4, 127.06) * mm, "end": v(50.2, 135.39) * mm});
            skLineSegment(sketch, "E403", {"start": v(49.37, 119.9) * mm, "end": v(57.23, 129.02) * mm});
            skArc(sketch, "E404", {"start": v(48.67, 212.22) * mm, "mid": v(44.97, 206.4) * mm, "end": v(42, 200.18) * mm});
            skArc(sketch, "E405.trimOffspring", {"start": v(58.67, 133.96) * mm, "mid": v(61.92, 131.46) * mm, "end": v(65.33, 129.2) * mm});
            skArc(sketch, "E406.trimOffspring", {"start": v(42, 156.7) * mm, "mid": v(44.97, 150.47) * mm, "end": v(48.67, 144.65) * mm});
            skArc(sketch, "E407.trimOffspring", {"start": v(65.33, 227.68) * mm, "mid": v(61.92, 225.42) * mm, "end": v(58.67, 222.91) * mm});
            skArc(sketch, "E408.trimOffspring", {"start": v(82, 234.59) * mm, "mid": v(78.64, 233.67) * mm, "end": v(75.33, 232.55) * mm});
            skArc(sketch, "E409.trimOffspring", {"start": v(98.67, 236.1) * mm, "mid": v(95.33, 236.19) * mm, "end": v(92, 236.08) * mm});
            skArc(sketch, "E410.trimOffspring", {"start": v(115.33, 232.67) * mm, "mid": v(112.03, 233.77) * mm, "end": v(108.67, 234.66) * mm});
            skArc(sketch, "E411.trimOffspring", {"start": v(132, 223.19) * mm, "mid": v(128.75, 225.65) * mm, "end": v(125.33, 227.88) * mm});
            skArc(sketch, "E412.trimOffspring", {"start": v(148.67, 200.98) * mm, "mid": v(145.68, 207.03) * mm, "end": v(142, 212.68) * mm});
            skArc(sketch, "E413.trimOffspring", {"start": v(142, 144.19) * mm, "mid": v(145.68, 149.84) * mm, "end": v(148.67, 155.89) * mm});
            skArc(sketch, "E414.trimOffspring", {"start": v(125.33, 128.99) * mm, "mid": v(128.75, 131.22) * mm, "end": v(132, 133.68) * mm});
            skArc(sketch, "E415.trimOffspring", {"start": v(108.67, 122.2) * mm, "mid": v(112.03, 123.1) * mm, "end": v(115.33, 124.2) * mm});
            skArc(sketch, "E416.trimOffspring", {"start": v(92, 120.8) * mm, "mid": v(95.33, 120.69) * mm, "end": v(98.67, 120.77) * mm});
            skArc(sketch, "E417.trimOffspring", {"start": v(75.33, 124.32) * mm, "mid": v(78.64, 123.2) * mm, "end": v(82, 122.29) * mm});
            skSolve(sketch);
        }
        {
            var Q0;
            Q0 = qSketchRegion(id + "F4", true);
            extrude(context, id + "F5", {"entities" : qUnion([Q0]), "depth" : 2 * mm});
        }
    });
